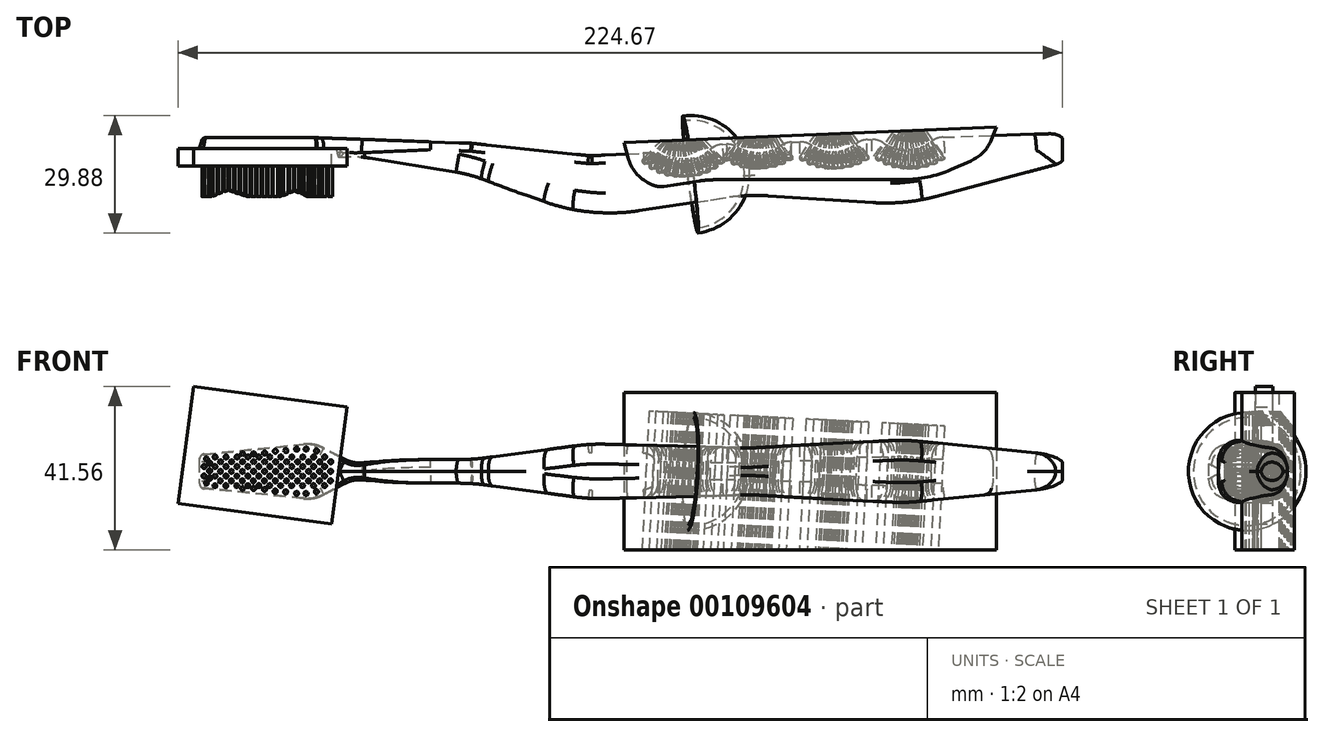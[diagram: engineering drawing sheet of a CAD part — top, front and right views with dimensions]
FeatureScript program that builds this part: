
annotation { "Feature Type Name" : "Feature", "Feature Type Description" : "" }
export const myFeature = defineFeature(function(context is Context, id is Id, definition is map)
    precondition{}
    {
        {
            var Q0;
            Q0=qCreatedBy(makeId("Front.planeOp"),FACE);
            var sketch = newSketch(context, id + "F0", { "sketchPlane" : qUnion([Q0])});
            skLineSegment(sketch, "E0", {"start": v(0, 0) * mm, "end": v(-220, 0) * mm, "construction": true});
            skLineSegment(sketch, "E1", {"start": v(-220, 0) * mm, "end": v(-220, 5) * mm});
            skLineSegment(sketch, "E2", {"start": v(-190, 0) * mm, "end": v(-190, 8) * mm, "construction": true});
            skLineSegment(sketch, "E3", {"start": v(-180, 0) * mm, "end": v(-180, 3) * mm, "construction": true});
            skLineSegment(sketch, "E4", {"start": v(-150, 0) * mm, "end": v(-150, 3) * mm, "construction": true});
            skLineSegment(sketch, "E5", {"start": v(-120, 0) * mm, "end": v(-120, 7) * mm, "construction": true});
            skLineSegment(sketch, "E6", {"start": v(-80, 0) * mm, "end": v(-80, 6) * mm, "construction": true});
            skLineSegment(sketch, "E7", {"start": v(-40, 0) * mm, "end": v(-40, 8) * mm, "construction": true});
            skLineSegment(sketch, "E8", {"start": v(0, 0) * mm, "end": v(0, 4) * mm});
            skLineSegment(sketch, "E9", {"start": v(0, 4) * mm, "end": v(-40, 8) * mm});
            skLineSegment(sketch, "E10", {"start": v(-40, 8) * mm, "end": v(-80, 6) * mm});
            skLineSegment(sketch, "E11", {"start": v(-80, 6) * mm, "end": v(-120, 7) * mm});
            skLineSegment(sketch, "E12", {"start": v(-120, 7) * mm, "end": v(-150, 3) * mm});
            skLineSegment(sketch, "E13", {"start": v(-150, 3) * mm, "end": v(-180, 3) * mm});
            skLineSegment(sketch, "E14", {"start": v(-180, 3) * mm, "end": v(-190, 8) * mm});
            skLineSegment(sketch, "E15", {"start": v(-190, 8) * mm, "end": v(-220, 5) * mm});
            skLineSegment(sketch, "E16.MirrorCS", {"start": v(0, 0) * mm, "end": v(0, -4) * mm});
            skLineSegment(sketch, "E17.MirrorCS", {"start": v(-220, 0) * mm, "end": v(-220, -5) * mm});
            skLineSegment(sketch, "E18.MirrorCS", {"start": v(-190, -8) * mm, "end": v(-220, -5) * mm});
            skLineSegment(sketch, "E19.MirrorCS", {"start": v(-180, -3) * mm, "end": v(-190, -8) * mm});
            skLineSegment(sketch, "E20.MirrorCS", {"start": v(-150, -3) * mm, "end": v(-180, -3) * mm});
            skLineSegment(sketch, "E21.MirrorCS", {"start": v(-120, -7) * mm, "end": v(-150, -3) * mm});
            skLineSegment(sketch, "E22.MirrorCS", {"start": v(-80, -6) * mm, "end": v(-120, -7) * mm});
            skLineSegment(sketch, "E23.MirrorCS", {"start": v(0, -4) * mm, "end": v(-40, -8) * mm});
            skLineSegment(sketch, "E24.MirrorCS", {"start": v(-40, -8) * mm, "end": v(-80, -6) * mm});
            skSolve(sketch);
        }
        {
            var Q0;
            Q0=makeQuery(id+"F0.imprint","IMPRINT",FACE,{"disambiguationData":[TD([[makeQuery(id+"F0.imprint","IMPRINT",EDGE,{"derivedFrom":sQuery(id+"F0.wireOp",EDGE,"E1")}),-1.0]])]});
            extrude(context, id + "F1", {"entities" : qUnion([Q0]), "depth" : 25 * mm});
        }
        {
            var Q0;
            Q0=makeQuery(id+"F1.opExtrude","SWEPT_FACE",FACE,{"disambiguationData":[OSD([sQuery(id+"F0.wireOp",EDGE,"E20.MirrorCS")])]});
            var sketch = newSketch(context, id + "F2", { "sketchPlane" : qUnion([Q0])});
            skLineSegment(sketch, "E25.0", {"start": v(-190, 0) * mm, "end": v(-220, 0) * mm, "construction": true});
            skLineSegment(sketch, "E25.4", {"start": v(-80, 0) * mm, "end": v(-120, 0) * mm, "construction": true});
            skLineSegment(sketch, "E25.5", {"start": v(-40, 0) * mm, "end": v(-80, 0) * mm, "construction": true});
            skLineSegment(sketch, "E25.6", {"start": v(0, 0) * mm, "end": v(-40, 0) * mm, "construction": true});
            skLineSegment(sketch, "E26", {"start": v(-220, 7.68) * mm, "end": v(-218.46, 2.68) * mm});
            skLineSegment(sketch, "E27", {"start": v(-218.46, 2.68) * mm, "end": v(-190, 2.68) * mm});
            skLineSegment(sketch, "E28", {"start": v(-119.9, 7.3) * mm, "end": v(-102.9, 6.47) * mm});
            skLineSegment(sketch, "E29", {"start": v(-119.9, 23.1) * mm, "end": v(-80, 17.11) * mm});
            skLineSegment(sketch, "E30", {"start": v(-80, 17.11) * mm, "end": v(-40, 19.71) * mm});
            skLineSegment(sketch, "E31", {"start": v(-40, 19.71) * mm, "end": v(0, 9.1) * mm});
            skLineSegment(sketch, "E32", {"start": v(0, 9.1) * mm, "end": v(0, 1.58) * mm});
            skArc(sketch, "E33", {"start": v(-88.51, 4.45) * mm, "mid": v(-95.27, 8.57) * mm, "end": v(-102.9, 6.47) * mm});
            skArc(sketch, "E34", {"start": v(-32.26, 2.63) * mm, "mid": v(-39.34, 5.9) * mm, "end": v(-46.62, 3.1) * mm});
            skLineSegment(sketch, "E35", {"start": v(-88.51, 4.45) * mm, "end": v(-83.73, 4.3) * mm});
            skLineSegment(sketch, "E36", {"start": v(-70.5, 3.87) * mm, "end": v(-64.85, 3.69) * mm});
            skArc(sketch, "E37.trimOffspring", {"start": v(-70.5, 3.87) * mm, "mid": v(-77.03, 6.54) * mm, "end": v(-83.73, 4.3) * mm});
            skLineSegment(sketch, "E38.trimOffspring", {"start": v(-51.47, 3.25) * mm, "end": v(-46.62, 3.1) * mm});
            skLineSegment(sketch, "E39.trimOffspring", {"start": v(-32.26, 2.63) * mm, "end": v(0, 1.58) * mm});
            skArc(sketch, "E40.trimOffspring", {"start": v(-51.47, 3.25) * mm, "mid": v(-58.07, 6.39) * mm, "end": v(-64.85, 3.69) * mm});
            skPoint(sketch, "E41.center.orphan", {"position": v(-77.66, -2.25) * mm});
            skPoint(sketch, "E42.center.orphan", {"position": v(-58.66, -3.17) * mm});
            skLineSegment(sketch, "E43.top", {"start": v(-229.41, 31.75) * mm, "end": v(15.55, 31.75) * mm});
            skLineSegment(sketch, "E43.left", {"start": v(-229.41, -17.07) * mm, "end": v(-229.41, 31.75) * mm});
            skLineSegment(sketch, "E43.right", {"start": v(15.55, -17.07) * mm, "end": v(15.55, 31.75) * mm});
            skLineSegment(sketch, "E44", {"start": v(-220, 7.68) * mm, "end": v(-180, 7.68) * mm});
            skLineSegment(sketch, "E45", {"start": v(-180, 7.68) * mm, "end": v(-150, 12.5) * mm});
            skLineSegment(sketch, "E46", {"start": v(-150, 12.5) * mm, "end": v(-119.9, 23.1) * mm});
            skLineSegment(sketch, "E47", {"start": v(-119.9, 7.3) * mm, "end": v(-150, 4.12) * mm});
            skLineSegment(sketch, "E48", {"start": v(-150, 4.12) * mm, "end": v(-190, 2.68) * mm});
            skLineSegment(sketch, "E49", {"start": v(15.55, -17.07) * mm, "end": v(-229.41, -17.07) * mm});
            skSolve(sketch);
        }
        {
            var Q0;
            Q0=makeQuery(id+"F2.imprint","IMPRINT",FACE,{"disambiguationData":[TD([[makeQuery(id+"F2.imprint","IMPRINT",EDGE,{"derivedFrom":sQuery(id+"F2.wireOp",EDGE,"E26")}),-1.0]])]});
            var Q1;
            {var subQ0=sQuery(id+"F2.wireOp",EDGE,"E45");Q1=makeQuery(id+"F2.imprint","IMPRINT",FACE,{"disambiguationData":[TD([[makeQuery(id+"F2.imprint","IMPRINT",EDGE,{"derivedFrom":subQ0}),1.0]])]});}
            var Q2;
            {var subQ1=sQuery(id+"F0.wireOp",EDGE,"E20.MirrorCS");var subQ6=makeQuery(id+"F1.opExtrude","CAP_EDGE",EDGE,{"disambiguationData":[OSD([subQ1])],"isStart":true});Q2=makeQuery(id+"F2.imprint","IMPRINT",FACE,{"disambiguationData":[TD([[makeQuery(id+"F2.imprint","IMPRINT",EDGE,{"derivedFrom":subQ6}),-1.0]])]});}
            extrude(context, id + "F3", {"entities" : qUnion([Q0, Q1, Q2]), "operationType" : NewBodyOperationType.REMOVE, "endBound" : BoundingType.SYMMETRIC, "oppositeDirection" : true, "depth" : 40 * mm});
        }
        {
            var Q0;
            Q0=makeQuery(id+"F3.boolean.opBoolean","COPY",EDGE,{"derivedFrom":makeQuery(id+"F3.opExtrude","SWEPT_EDGE",EDGE,{"disambiguationData":[OSD([sQuery(id+"F2.wireOp",EDGE,"E29"),sQuery(id+"F2.wireOp",EDGE,"E46")])]})});
            var Q1;
            Q1=makeQuery(id+"F3.boolean.opBoolean","COPY",EDGE,{"derivedFrom":makeQuery(id+"F3.opExtrude","SWEPT_EDGE",EDGE,{"disambiguationData":[OSD([sQuery(id+"F2.wireOp",EDGE,"E29"),sQuery(id+"F2.wireOp",EDGE,"E30")])]})});
            var Q2;
            Q2=makeQuery(id+"F3.boolean.opBoolean","COPY",EDGE,{"derivedFrom":makeQuery(id+"F3.opExtrude","SWEPT_EDGE",EDGE,{"disambiguationData":[OSD([sQuery(id+"F2.wireOp",EDGE,"E30"),sQuery(id+"F2.wireOp",EDGE,"E31")])]})});
            var Q3;
            Q3=makeQuery(id+"F3.boolean.opBoolean","COPY",EDGE,{"derivedFrom":makeQuery(id+"F3.opExtrude","SWEPT_EDGE",EDGE,{"disambiguationData":[OSD([sQuery(id+"F0.wireOp",EDGE,"E20.MirrorCS"),sQuery(id+"F0.wireOp",EDGE,"E21.MirrorCS"),sQuery(id+"F2.wireOp",EDGE,"E45"),sQuery(id+"F2.wireOp",EDGE,"E46")])]})});
            var Q4;
            Q4=makeQuery(id+"F3.boolean.opBoolean","COPY",EDGE,{"derivedFrom":makeQuery(id+"F3.opExtrude","SWEPT_EDGE",EDGE,{"disambiguationData":[OSD([sQuery(id+"F0.wireOp",EDGE,"E19.MirrorCS"),sQuery(id+"F0.wireOp",EDGE,"E20.MirrorCS"),sQuery(id+"F2.wireOp",EDGE,"E44"),sQuery(id+"F2.wireOp",EDGE,"E45")])]})});
            fillet(context, id + "F4", {"entities" : qUnion([Q0, Q1, Q2, Q3, Q4]), "radius" : 50 * mm, "tangentPropagation" : true, "allowEdgeOverflow" : false});
        }
        {
            var Q0;
            Q0=makeQuery(id+"F3.boolean.opBoolean","COPY",EDGE,{"derivedFrom":makeQuery(id+"F3.opExtrude","SWEPT_EDGE",EDGE,{"disambiguationData":[OSD([sQuery(id+"F2.wireOp",EDGE,"E27"),sQuery(id+"F2.wireOp",EDGE,"E48")])]})});
            var Q1;
            Q1=makeQuery(id+"F3.boolean.opBoolean","COPY",EDGE,{"derivedFrom":makeQuery(id+"F3.opExtrude","SWEPT_EDGE",EDGE,{"disambiguationData":[OSD([sQuery(id+"F0.wireOp",EDGE,"E20.MirrorCS"),sQuery(id+"F0.wireOp",EDGE,"E21.MirrorCS"),sQuery(id+"F2.wireOp",EDGE,"E47"),sQuery(id+"F2.wireOp",EDGE,"E48")])]})});
            var Q2;
            Q2=makeQuery(id+"F3.boolean.opBoolean","COPY",EDGE,{"derivedFrom":makeQuery(id+"F3.opExtrude","SWEPT_EDGE",EDGE,{"disambiguationData":[OSD([sQuery(id+"F2.wireOp",EDGE,"E28"),sQuery(id+"F2.wireOp",EDGE,"E47")])]})});
            fillet(context, id + "F5", {"entities" : qUnion([Q0, Q1, Q2]), "radius" : 5 * mm, "tangentPropagation" : true, "allowEdgeOverflow" : false});
        }
        {
            var Q0;
            Q0=makeQuery(id+"F1.opExtrude","SWEPT_EDGE",EDGE,{"disambiguationData":[OSD([sQuery(id+"F0.wireOp",EDGE,"E20.MirrorCS"),sQuery(id+"F0.wireOp",EDGE,"E21.MirrorCS")])]});
            var Q1;
            Q1=makeQuery(id+"F1.opExtrude","SWEPT_EDGE",EDGE,{"disambiguationData":[OSD([sQuery(id+"F0.wireOp",EDGE,"E21.MirrorCS"),sQuery(id+"F0.wireOp",EDGE,"E22.MirrorCS")])]});
            var Q2;
            Q2=makeQuery(id+"F1.opExtrude","SWEPT_EDGE",EDGE,{"disambiguationData":[OSD([sQuery(id+"F0.wireOp",EDGE,"E22.MirrorCS"),sQuery(id+"F0.wireOp",EDGE,"E24.MirrorCS")])]});
            var Q3;
            Q3=makeQuery(id+"F1.opExtrude","SWEPT_EDGE",EDGE,{"disambiguationData":[OSD([sQuery(id+"F0.wireOp",EDGE,"E23.MirrorCS"),sQuery(id+"F0.wireOp",EDGE,"E24.MirrorCS")])]});
            var Q4;
            Q4=makeQuery(id+"F1.opExtrude","SWEPT_EDGE",EDGE,{"disambiguationData":[OSD([sQuery(id+"F0.wireOp",EDGE,"E12"),sQuery(id+"F0.wireOp",EDGE,"E13")])]});
            var Q5;
            Q5=makeQuery(id+"F1.opExtrude","SWEPT_EDGE",EDGE,{"disambiguationData":[OSD([sQuery(id+"F0.wireOp",EDGE,"E11"),sQuery(id+"F0.wireOp",EDGE,"E12")])]});
            var Q6;
            Q6=makeQuery(id+"F1.opExtrude","SWEPT_EDGE",EDGE,{"disambiguationData":[OSD([sQuery(id+"F0.wireOp",EDGE,"E10"),sQuery(id+"F0.wireOp",EDGE,"E11")])]});
            var Q7;
            Q7=makeQuery(id+"F1.opExtrude","SWEPT_EDGE",EDGE,{"disambiguationData":[OSD([sQuery(id+"F0.wireOp",EDGE,"E9"),sQuery(id+"F0.wireOp",EDGE,"E10")])]});
            fillet(context, id + "F6", {"entities" : qUnion([Q0, Q1, Q2, Q3, Q4, Q5, Q6, Q7]), "radius" : 50 * mm, "tangentPropagation" : true, "allowEdgeOverflow" : false});
        }
        {
            var Q0;
            Q0=makeQuery(id+"F1.opExtrude","SWEPT_EDGE",EDGE,{"disambiguationData":[OSD([sQuery(id+"F0.wireOp",EDGE,"E18.MirrorCS"),sQuery(id+"F0.wireOp",EDGE,"E19.MirrorCS")])]});
            var Q1;
            Q1=makeQuery(id+"F1.opExtrude","SWEPT_EDGE",EDGE,{"disambiguationData":[OSD([sQuery(id+"F0.wireOp",EDGE,"E19.MirrorCS"),sQuery(id+"F0.wireOp",EDGE,"E20.MirrorCS")])]});
            var Q2;
            Q2=makeQuery(id+"F1.opExtrude","SWEPT_EDGE",EDGE,{"disambiguationData":[OSD([sQuery(id+"F0.wireOp",EDGE,"E13"),sQuery(id+"F0.wireOp",EDGE,"E14")])]});
            var Q3;
            Q3=makeQuery(id+"F1.opExtrude","SWEPT_EDGE",EDGE,{"disambiguationData":[OSD([sQuery(id+"F0.wireOp",EDGE,"E14"),sQuery(id+"F0.wireOp",EDGE,"E15")])]});
            fillet(context, id + "F7", {"entities" : qUnion([Q0, Q1, Q2, Q3]), "radius" : 10 * mm, "tangentPropagation" : true, "allowEdgeOverflow" : false});
        }
        {
            var Q0;
            Q0=makeQuery(id+"F6.opFillet","BLEND_EDGE",EDGE,{"blendedFrom":[makeQuery(id+"F1.opExtrude","SWEPT_EDGE",EDGE,{"disambiguationData":[OSD([sQuery(id+"F0.wireOp",EDGE,"E21.MirrorCS"),sQuery(id+"F0.wireOp",EDGE,"E22.MirrorCS")])]}),makeQuery(id+"F4.opFillet","BLEND_FACE",FACE,{"disambiguationData":[OSD([sQuery(id+"F2.wireOp",EDGE,"E29"),sQuery(id+"F2.wireOp",EDGE,"E46")])]})],"blendedInto":[makeQuery(id+"F4.opFillet","BLEND_FACE",FACE,{"disambiguationData":[OSD([sQuery(id+"F2.wireOp",EDGE,"E29"),sQuery(id+"F2.wireOp",EDGE,"E46")])]})]});
            var Q1;
            Q1=makeQuery(id+"F3.boolean.opBoolean","INTERSECT",EDGE,{"derivedFrom":[makeQuery(id+"F1.opExtrude","SWEPT_FACE",FACE,{"disambiguationData":[OSD([sQuery(id+"F0.wireOp",EDGE,"E11")])]}),makeQuery(id+"F3.opExtrude","SWEPT_FACE",FACE,{"disambiguationData":[OSD([sQuery(id+"F2.wireOp",EDGE,"E29")])]})]});
            fillet(context, id + "F8", {"entities" : qUnion([Q0, Q1]), "radius" : 5 * mm, "tangentPropagation" : true, "allowEdgeOverflow" : false});
        }
        {
            var Q0;
            Q0=makeQuery(id+"F3.boolean.opBoolean","INTERSECT",EDGE,{"derivedFrom":[makeQuery(id+"F1.opExtrude","SWEPT_FACE",FACE,{"disambiguationData":[OSD([sQuery(id+"F0.wireOp",EDGE,"E22.MirrorCS")])]}),makeQuery(id+"F3.opExtrude","SWEPT_FACE",FACE,{"disambiguationData":[OSD([sQuery(id+"F2.wireOp",EDGE,"E33")])]})]});
            var Q1;
            Q1=makeQuery(id+"F6.opFillet","BLEND_EDGE",EDGE,{"blendedFrom":[makeQuery(id+"F1.opExtrude","SWEPT_EDGE",EDGE,{"disambiguationData":[OSD([sQuery(id+"F0.wireOp",EDGE,"E22.MirrorCS"),sQuery(id+"F0.wireOp",EDGE,"E24.MirrorCS")])]}),makeQuery(id+"F3.boolean.opBoolean","COPY",FACE,{"derivedFrom":makeQuery(id+"F3.opExtrude","SWEPT_FACE",FACE,{"disambiguationData":[OSD([sQuery(id+"F2.wireOp",EDGE,"E37.trimOffspring")])]})})],"blendedInto":[makeQuery(id+"F3.boolean.opBoolean","COPY",FACE,{"derivedFrom":makeQuery(id+"F3.opExtrude","SWEPT_FACE",FACE,{"disambiguationData":[OSD([sQuery(id+"F2.wireOp",EDGE,"E37.trimOffspring")])]})})]});
            var Q2;
            Q2=makeQuery(id+"F3.boolean.opBoolean","INTERSECT",EDGE,{"derivedFrom":[makeQuery(id+"F1.opExtrude","SWEPT_FACE",FACE,{"disambiguationData":[OSD([sQuery(id+"F0.wireOp",EDGE,"E24.MirrorCS")])]}),makeQuery(id+"F3.opExtrude","SWEPT_FACE",FACE,{"disambiguationData":[OSD([sQuery(id+"F2.wireOp",EDGE,"E40.trimOffspring")])]})]});
            var Q3;
            Q3=makeQuery(id+"F6.opFillet","BLEND_EDGE",EDGE,{"blendedFrom":[makeQuery(id+"F1.opExtrude","SWEPT_EDGE",EDGE,{"disambiguationData":[OSD([sQuery(id+"F0.wireOp",EDGE,"E23.MirrorCS"),sQuery(id+"F0.wireOp",EDGE,"E24.MirrorCS")])]}),makeQuery(id+"F3.boolean.opBoolean","COPY",FACE,{"derivedFrom":makeQuery(id+"F3.opExtrude","SWEPT_FACE",FACE,{"disambiguationData":[OSD([sQuery(id+"F2.wireOp",EDGE,"E34")])]})})],"blendedInto":[makeQuery(id+"F3.boolean.opBoolean","COPY",FACE,{"derivedFrom":makeQuery(id+"F3.opExtrude","SWEPT_FACE",FACE,{"disambiguationData":[OSD([sQuery(id+"F2.wireOp",EDGE,"E34")])]})})]});
            var Q4;
            Q4=makeQuery(id+"F3.boolean.opBoolean","INTERSECT",EDGE,{"derivedFrom":[makeQuery(id+"F1.opExtrude","SWEPT_FACE",FACE,{"disambiguationData":[OSD([sQuery(id+"F0.wireOp",EDGE,"E22.MirrorCS")])]}),makeQuery(id+"F3.opExtrude","SWEPT_FACE",FACE,{"disambiguationData":[OSD([sQuery(id+"F2.wireOp",EDGE,"E35")])]})]});
            var Q5;
            Q5=makeQuery(id+"F3.boolean.opBoolean","INTERSECT",EDGE,{"derivedFrom":[makeQuery(id+"F1.opExtrude","SWEPT_FACE",FACE,{"disambiguationData":[OSD([sQuery(id+"F0.wireOp",EDGE,"E24.MirrorCS")])]}),makeQuery(id+"F3.opExtrude","SWEPT_FACE",FACE,{"disambiguationData":[OSD([sQuery(id+"F2.wireOp",EDGE,"E36")])]})]});
            var Q6;
            Q6=makeQuery(id+"F3.boolean.opBoolean","INTERSECT",EDGE,{"derivedFrom":[makeQuery(id+"F1.opExtrude","SWEPT_FACE",FACE,{"disambiguationData":[OSD([sQuery(id+"F0.wireOp",EDGE,"E24.MirrorCS")])]}),makeQuery(id+"F3.opExtrude","SWEPT_FACE",FACE,{"disambiguationData":[OSD([sQuery(id+"F2.wireOp",EDGE,"E38.trimOffspring")])]})]});
            var Q7;
            Q7=makeQuery(id+"F3.boolean.opBoolean","INTERSECT",EDGE,{"derivedFrom":[makeQuery(id+"F1.opExtrude","SWEPT_FACE",FACE,{"disambiguationData":[OSD([sQuery(id+"F0.wireOp",EDGE,"E23.MirrorCS")])]}),makeQuery(id+"F3.opExtrude","SWEPT_FACE",FACE,{"disambiguationData":[OSD([sQuery(id+"F2.wireOp",EDGE,"E39.trimOffspring")])]})]});
            var Q8;
            Q8=makeQuery(id+"F3.boolean.opBoolean","INTERSECT",EDGE,{"derivedFrom":[makeQuery(id+"F1.opExtrude","SWEPT_FACE",FACE,{"disambiguationData":[OSD([sQuery(id+"F0.wireOp",EDGE,"E11")])]}),makeQuery(id+"F3.opExtrude","SWEPT_FACE",FACE,{"disambiguationData":[OSD([sQuery(id+"F2.wireOp",EDGE,"E33")])]})]});
            var Q9;
            Q9=makeQuery(id+"F3.boolean.opBoolean","INTERSECT",EDGE,{"derivedFrom":[makeQuery(id+"F1.opExtrude","SWEPT_FACE",FACE,{"disambiguationData":[OSD([sQuery(id+"F0.wireOp",EDGE,"E11")])]}),makeQuery(id+"F3.opExtrude","SWEPT_FACE",FACE,{"disambiguationData":[OSD([sQuery(id+"F2.wireOp",EDGE,"E35")])]})]});
            var Q10;
            Q10=makeQuery(id+"F3.boolean.opBoolean","INTERSECT",EDGE,{"derivedFrom":[makeQuery(id+"F1.opExtrude","SWEPT_FACE",FACE,{"disambiguationData":[OSD([sQuery(id+"F0.wireOp",EDGE,"E10")])]}),makeQuery(id+"F3.opExtrude","SWEPT_FACE",FACE,{"disambiguationData":[OSD([sQuery(id+"F2.wireOp",EDGE,"E37.trimOffspring")])]})]});
            var Q11;
            Q11=makeQuery(id+"F3.boolean.opBoolean","INTERSECT",EDGE,{"derivedFrom":[makeQuery(id+"F1.opExtrude","SWEPT_FACE",FACE,{"disambiguationData":[OSD([sQuery(id+"F0.wireOp",EDGE,"E10")])]}),makeQuery(id+"F3.opExtrude","SWEPT_FACE",FACE,{"disambiguationData":[OSD([sQuery(id+"F2.wireOp",EDGE,"E36")])]})]});
            var Q12;
            Q12=makeQuery(id+"F3.boolean.opBoolean","INTERSECT",EDGE,{"derivedFrom":[makeQuery(id+"F1.opExtrude","SWEPT_FACE",FACE,{"disambiguationData":[OSD([sQuery(id+"F0.wireOp",EDGE,"E10")])]}),makeQuery(id+"F3.opExtrude","SWEPT_FACE",FACE,{"disambiguationData":[OSD([sQuery(id+"F2.wireOp",EDGE,"E40.trimOffspring")])]})]});
            var Q13;
            Q13=makeQuery(id+"F3.boolean.opBoolean","INTERSECT",EDGE,{"derivedFrom":[makeQuery(id+"F1.opExtrude","SWEPT_FACE",FACE,{"disambiguationData":[OSD([sQuery(id+"F0.wireOp",EDGE,"E10")])]}),makeQuery(id+"F3.opExtrude","SWEPT_FACE",FACE,{"disambiguationData":[OSD([sQuery(id+"F2.wireOp",EDGE,"E38.trimOffspring")])]})]});
            var Q14;
            Q14=makeQuery(id+"F6.opFillet","BLEND_EDGE",EDGE,{"blendedFrom":[makeQuery(id+"F1.opExtrude","SWEPT_EDGE",EDGE,{"disambiguationData":[OSD([sQuery(id+"F0.wireOp",EDGE,"E9"),sQuery(id+"F0.wireOp",EDGE,"E10")])]}),makeQuery(id+"F3.boolean.opBoolean","COPY",FACE,{"derivedFrom":makeQuery(id+"F3.opExtrude","SWEPT_FACE",FACE,{"disambiguationData":[OSD([sQuery(id+"F2.wireOp",EDGE,"E34")])]})})],"blendedInto":[makeQuery(id+"F3.boolean.opBoolean","COPY",FACE,{"derivedFrom":makeQuery(id+"F3.opExtrude","SWEPT_FACE",FACE,{"disambiguationData":[OSD([sQuery(id+"F2.wireOp",EDGE,"E34")])]})})]});
            var Q15;
            Q15=makeQuery(id+"F3.boolean.opBoolean","INTERSECT",EDGE,{"derivedFrom":[makeQuery(id+"F1.opExtrude","SWEPT_FACE",FACE,{"disambiguationData":[OSD([sQuery(id+"F0.wireOp",EDGE,"E9")])]}),makeQuery(id+"F3.opExtrude","SWEPT_FACE",FACE,{"disambiguationData":[OSD([sQuery(id+"F2.wireOp",EDGE,"E39.trimOffspring")])]})]});
            fillet(context, id + "F9", {"entities" : qUnion([Q0, Q1, Q2, Q3, Q4, Q5, Q6, Q7, Q8, Q9, Q10, Q11, Q12, Q13, Q14, Q15]), "radius" : 4 * mm, "tangentPropagation" : true, "allowEdgeOverflow" : false});
        }
        {
            var Q0;
            Q0=makeQuery(id+"F3.boolean.opBoolean","INTERSECT",EDGE,{"derivedFrom":[makeQuery(id+"F1.opExtrude","SWEPT_FACE",FACE,{"disambiguationData":[OSD([sQuery(id+"F0.wireOp",EDGE,"E22.MirrorCS")])]}),makeQuery(id+"F3.opExtrude","SWEPT_FACE",FACE,{"disambiguationData":[OSD([sQuery(id+"F2.wireOp",EDGE,"E28")])]})]});
            fillet(context, id + "F10", {"entities" : qUnion([Q0]), "radius" : 2 * mm, "tangentPropagation" : true, "allowEdgeOverflow" : false});
        }
        {
            var Q0;
            Q0=makeQuery(id+"F3.boolean.opBoolean","COPY",EDGE,{"derivedFrom":makeQuery(id+"F3.opExtrude","SWEPT_EDGE",EDGE,{"disambiguationData":[OSD([sQuery(id+"F2.wireOp",EDGE,"E33"),sQuery(id+"F2.wireOp",EDGE,"E35")])]})});
            var Q1;
            Q1=makeQuery(id+"F3.boolean.opBoolean","COPY",EDGE,{"derivedFrom":makeQuery(id+"F3.opExtrude","SWEPT_EDGE",EDGE,{"disambiguationData":[OSD([sQuery(id+"F2.wireOp",EDGE,"E35"),sQuery(id+"F2.wireOp",EDGE,"E37.trimOffspring")])]})});
            var Q2;
            Q2=makeQuery(id+"F3.boolean.opBoolean","COPY",EDGE,{"derivedFrom":makeQuery(id+"F3.opExtrude","SWEPT_EDGE",EDGE,{"disambiguationData":[OSD([sQuery(id+"F2.wireOp",EDGE,"E36"),sQuery(id+"F2.wireOp",EDGE,"E37.trimOffspring")])]})});
            var Q3;
            Q3=makeQuery(id+"F3.boolean.opBoolean","COPY",EDGE,{"derivedFrom":makeQuery(id+"F3.opExtrude","SWEPT_EDGE",EDGE,{"disambiguationData":[OSD([sQuery(id+"F2.wireOp",EDGE,"E36"),sQuery(id+"F2.wireOp",EDGE,"E40.trimOffspring")])]})});
            var Q4;
            Q4=makeQuery(id+"F3.boolean.opBoolean","COPY",EDGE,{"derivedFrom":makeQuery(id+"F3.opExtrude","SWEPT_EDGE",EDGE,{"disambiguationData":[OSD([sQuery(id+"F2.wireOp",EDGE,"E38.trimOffspring"),sQuery(id+"F2.wireOp",EDGE,"E40.trimOffspring")])]})});
            var Q5;
            Q5=makeQuery(id+"F3.boolean.opBoolean","COPY",EDGE,{"derivedFrom":makeQuery(id+"F3.opExtrude","SWEPT_EDGE",EDGE,{"disambiguationData":[OSD([sQuery(id+"F2.wireOp",EDGE,"E34"),sQuery(id+"F2.wireOp",EDGE,"E38.trimOffspring")])]})});
            var Q6;
            Q6=makeQuery(id+"F3.boolean.opBoolean","COPY",EDGE,{"derivedFrom":makeQuery(id+"F3.opExtrude","SWEPT_EDGE",EDGE,{"disambiguationData":[OSD([sQuery(id+"F2.wireOp",EDGE,"E34"),sQuery(id+"F2.wireOp",EDGE,"E39.trimOffspring")])]})});
            fillet(context, id + "F11", {"entities" : qUnion([Q0, Q1, Q2, Q3, Q4, Q5, Q6]), "radius" : 5 * mm, "tangentPropagation" : true, "allowEdgeOverflow" : false});
        }
        {
            var Q0;
            Q0=makeQuery(id+"F8.opFillet","BLEND_EDGE",EDGE,{"blendedFrom":[makeQuery(id+"F3.boolean.opBoolean","INTERSECT",EDGE,{"derivedFrom":[makeQuery(id+"F1.opExtrude","SWEPT_FACE",FACE,{"disambiguationData":[OSD([sQuery(id+"F0.wireOp",EDGE,"E18.MirrorCS")])]}),makeQuery(id+"F3.opExtrude","SWEPT_FACE",FACE,{"disambiguationData":[OSD([sQuery(id+"F2.wireOp",EDGE,"E44")])]})]}),makeQuery(id+"F3.boolean.opBoolean","COPY",FACE,{"derivedFrom":makeQuery(id+"F3.opExtrude","SWEPT_FACE",FACE,{"disambiguationData":[OSD([sQuery(id+"F2.wireOp",EDGE,"E26")])]})})],"blendedInto":[makeQuery(id+"F3.boolean.opBoolean","COPY",FACE,{"derivedFrom":makeQuery(id+"F3.opExtrude","SWEPT_FACE",FACE,{"disambiguationData":[OSD([sQuery(id+"F2.wireOp",EDGE,"E26")])]})})]});
            fillet(context, id + "F12", {"entities" : qUnion([Q0]), "radius" : 1 * mm, "tangentPropagation" : true, "allowEdgeOverflow" : false});
        }
        {
            var Q0;
            Q0=qCreatedBy(makeId("Top.planeOp"),FACE);
            var sketch = newSketch(context, id + "F13", { "sketchPlane" : qUnion([Q0])});
            skLineSegment(sketch, "E50", {"start": v(-111.36, -3.91) * mm, "end": v(-110.38, -7.71) * mm});
            skLineSegment(sketch, "E51", {"start": v(-104.93, -14.29) * mm, "end": v(-104.14, -14.66) * mm});
            skLineSegment(sketch, "E52", {"start": v(-101.27, -15.07) * mm, "end": v(-92.35, -13.7) * mm});
            skLineSegment(sketch, "E53", {"start": v(-87.82, -13.36) * mm, "end": v(-74.2, -13.36) * mm});
            skLineSegment(sketch, "E54", {"start": v(-74.2, -13.36) * mm, "end": v(-53.16, -13.36) * mm});
            skLineSegment(sketch, "E55", {"start": v(-53.16, -13.36) * mm, "end": v(-40.43, -13.36) * mm});
            skLineSegment(sketch, "E56", {"start": v(-28.35, -10.83) * mm, "end": v(-23.32, -8.61) * mm});
            skLineSegment(sketch, "E57", {"start": v(-18.04, -3.12) * mm, "end": v(-16.8, 0) * mm});
            skPoint(sketch, "E58.visualSharp", {"position": v(-109.21, -12.29) * mm});
            skArc(sketch, "E58.filletArc", {"start": v(-110.38, -7.71) * mm, "mid": v(-108.4, -11.61) * mm, "end": v(-104.93, -14.29) * mm});
            skPoint(sketch, "E59.visualSharp", {"position": v(-102.77, -15.3) * mm});
            skArc(sketch, "E59.filletArc", {"start": v(-104.14, -14.66) * mm, "mid": v(-102.74, -15.07) * mm, "end": v(-101.27, -15.07) * mm});
            skPoint(sketch, "E60.visualSharp", {"position": v(-19.55, -6.95) * mm});
            skArc(sketch, "E60.filletArc", {"start": v(-23.32, -8.61) * mm, "mid": v(-20.13, -6.39) * mm, "end": v(-18.04, -3.12) * mm});
            skPoint(sketch, "E61.visualSharp", {"position": v(-34.12, -13.36) * mm});
            skArc(sketch, "E61.filletArc", {"start": v(-40.43, -13.36) * mm, "mid": v(-34.26, -12.72) * mm, "end": v(-28.35, -10.83) * mm});
            skPoint(sketch, "E62.visualSharp", {"position": v(-90.1, -13.36) * mm});
            skArc(sketch, "E62.filletArc", {"start": v(-87.82, -13.36) * mm, "mid": v(-90.1, -13.45) * mm, "end": v(-92.35, -13.7) * mm});
            skLineSegment(sketch, "E63", {"start": v(-111.36, -3.91) * mm, "end": v(-16.8, 0) * mm});
            skSolve(sketch);
        }
        {
            var Q0;
            Q0=makeQuery(id+"F13.imprint","IMPRINT",FACE,{"disambiguationData":[TD([[makeQuery(id+"F13.imprint","IMPRINT",EDGE,{"derivedFrom":sQuery(id+"F13.wireOp",EDGE,"E50")}),1.0]])]});
            extrude(context, id + "F14", {"entities" : qUnion([Q0]), "endBound" : BoundingType.SYMMETRIC, "depth" : 40 * mm});
        }
        {
            var Q0;
            Q0=makeQuery(id+"F14.opExtrude","SWEPT_BODY",BODY,{"disambiguationData":[OSD([sQuery(id+"F13.wireOp",EDGE,"E50"),sQuery(id+"F13.wireOp",EDGE,"E51"),sQuery(id+"F13.wireOp",EDGE,"E52"),sQuery(id+"F13.wireOp",EDGE,"E53"),sQuery(id+"F13.wireOp",EDGE,"E54"),sQuery(id+"F13.wireOp",EDGE,"E55"),sQuery(id+"F13.wireOp",EDGE,"E56"),sQuery(id+"F13.wireOp",EDGE,"E57"),sQuery(id+"F13.wireOp",EDGE,"E58.filletArc"),sQuery(id+"F13.wireOp",EDGE,"E59.filletArc"),sQuery(id+"F13.wireOp",EDGE,"E60.filletArc"),sQuery(id+"F13.wireOp",EDGE,"E61.filletArc"),sQuery(id+"F13.wireOp",EDGE,"E62.filletArc"),sQuery(id+"F13.wireOp",EDGE,"E63")])]});
            var Q1;
            Q1=makeQuery(id+"F1.opExtrude","SWEPT_BODY",BODY,{"disambiguationData":[OSD([sQuery(id+"F0.wireOp",EDGE,"E1"),sQuery(id+"F0.wireOp",EDGE,"E8"),sQuery(id+"F0.wireOp",EDGE,"E9"),sQuery(id+"F0.wireOp",EDGE,"E10"),sQuery(id+"F0.wireOp",EDGE,"E11"),sQuery(id+"F0.wireOp",EDGE,"E12"),sQuery(id+"F0.wireOp",EDGE,"E13"),sQuery(id+"F0.wireOp",EDGE,"E14"),sQuery(id+"F0.wireOp",EDGE,"E15"),sQuery(id+"F0.wireOp",EDGE,"E16.MirrorCS"),sQuery(id+"F0.wireOp",EDGE,"E17.MirrorCS"),sQuery(id+"F0.wireOp",EDGE,"E18.MirrorCS"),sQuery(id+"F0.wireOp",EDGE,"E19.MirrorCS"),sQuery(id+"F0.wireOp",EDGE,"E20.MirrorCS"),sQuery(id+"F0.wireOp",EDGE,"E21.MirrorCS"),sQuery(id+"F0.wireOp",EDGE,"E22.MirrorCS"),sQuery(id+"F0.wireOp",EDGE,"E23.MirrorCS"),sQuery(id+"F0.wireOp",EDGE,"E24.MirrorCS")])]});
            booleanBodies(context, id + "F15", {"operationType" : BooleanOperationType.INTERSECTION, "tools" : qUnion([Q0, Q1]), "keepTools" : true});
        }
        {
            var Q0;
            Q0=makeQuery(id+"F15.opBoolean","INTERSECT",BODY,{"derivedFrom":[makeQuery(id+"F1.opExtrude","SWEPT_BODY",BODY,{"disambiguationData":[OSD([sQuery(id+"F0.wireOp",EDGE,"E1"),sQuery(id+"F0.wireOp",EDGE,"E8"),sQuery(id+"F0.wireOp",EDGE,"E9"),sQuery(id+"F0.wireOp",EDGE,"E10"),sQuery(id+"F0.wireOp",EDGE,"E11"),sQuery(id+"F0.wireOp",EDGE,"E12"),sQuery(id+"F0.wireOp",EDGE,"E13"),sQuery(id+"F0.wireOp",EDGE,"E14"),sQuery(id+"F0.wireOp",EDGE,"E15"),sQuery(id+"F0.wireOp",EDGE,"E16.MirrorCS"),sQuery(id+"F0.wireOp",EDGE,"E17.MirrorCS"),sQuery(id+"F0.wireOp",EDGE,"E18.MirrorCS"),sQuery(id+"F0.wireOp",EDGE,"E19.MirrorCS"),sQuery(id+"F0.wireOp",EDGE,"E20.MirrorCS"),sQuery(id+"F0.wireOp",EDGE,"E21.MirrorCS"),sQuery(id+"F0.wireOp",EDGE,"E22.MirrorCS"),sQuery(id+"F0.wireOp",EDGE,"E23.MirrorCS"),sQuery(id+"F0.wireOp",EDGE,"E24.MirrorCS")])]}),makeQuery(id+"F14.opExtrude","SWEPT_BODY",BODY,{"disambiguationData":[OSD([sQuery(id+"F13.wireOp",EDGE,"E50"),sQuery(id+"F13.wireOp",EDGE,"E51"),sQuery(id+"F13.wireOp",EDGE,"E52"),sQuery(id+"F13.wireOp",EDGE,"E53"),sQuery(id+"F13.wireOp",EDGE,"E54"),sQuery(id+"F13.wireOp",EDGE,"E55"),sQuery(id+"F13.wireOp",EDGE,"E56"),sQuery(id+"F13.wireOp",EDGE,"E57"),sQuery(id+"F13.wireOp",EDGE,"E58.filletArc"),sQuery(id+"F13.wireOp",EDGE,"E59.filletArc"),sQuery(id+"F13.wireOp",EDGE,"E60.filletArc"),sQuery(id+"F13.wireOp",EDGE,"E61.filletArc"),sQuery(id+"F13.wireOp",EDGE,"E62.filletArc"),sQuery(id+"F13.wireOp",EDGE,"E63")])]})]});
            var Q1;
            Q1=makeQuery(id+"F1.opExtrude","SWEPT_BODY",BODY,{"disambiguationData":[OSD([sQuery(id+"F0.wireOp",EDGE,"E1"),sQuery(id+"F0.wireOp",EDGE,"E8"),sQuery(id+"F0.wireOp",EDGE,"E9"),sQuery(id+"F0.wireOp",EDGE,"E10"),sQuery(id+"F0.wireOp",EDGE,"E11"),sQuery(id+"F0.wireOp",EDGE,"E12"),sQuery(id+"F0.wireOp",EDGE,"E13"),sQuery(id+"F0.wireOp",EDGE,"E14"),sQuery(id+"F0.wireOp",EDGE,"E15"),sQuery(id+"F0.wireOp",EDGE,"E16.MirrorCS"),sQuery(id+"F0.wireOp",EDGE,"E17.MirrorCS"),sQuery(id+"F0.wireOp",EDGE,"E18.MirrorCS"),sQuery(id+"F0.wireOp",EDGE,"E19.MirrorCS"),sQuery(id+"F0.wireOp",EDGE,"E20.MirrorCS"),sQuery(id+"F0.wireOp",EDGE,"E21.MirrorCS"),sQuery(id+"F0.wireOp",EDGE,"E22.MirrorCS"),sQuery(id+"F0.wireOp",EDGE,"E23.MirrorCS"),sQuery(id+"F0.wireOp",EDGE,"E24.MirrorCS")])]});
            booleanBodies(context, id + "F16", {"operationType" : BooleanOperationType.SUBTRACTION, "tools" : qUnion([Q0]), "targets" : qUnion([Q1]), "keepTools" : true});
        }
        {
            var Q0;
            Q0=makeQuery(id+"F15.opBoolean","COPY",FACE,{"derivedFrom":makeQuery(id+"F1.opExtrude","SWEPT_FACE",FACE,{"disambiguationData":[OSD([sQuery(id+"F0.wireOp",EDGE,"E24.MirrorCS")])]})});
            var sketch = newSketch(context, id + "F17", { "sketchPlane" : qUnion([Q0])});
            skEllipticalArc(sketch, "E64.0", {});
            skLineSegment(sketch, "E65", {"start": v(-96.12, -1.34) * mm, "end": v(-105.56, 8.28) * mm});
            skLineSegment(sketch, "E66", {"start": v(-96.12, -1.34) * mm, "end": v(-104.6, 9.15) * mm});
            skLineSegment(sketch, "E67.anchor1", {"start": v(-96.12, -1.34) * mm, "end": v(-96.12, -1.34) * mm});
            skLineSegment(sketch, "E67.anchor2", {"start": v(-96.12, -1.34) * mm, "end": v(-96.12, -1.34) * mm});
            skPoint(sketch, "E68.visualSharp", {"position": v(-104.91, 9.54) * mm});
            skArc(sketch, "E68.filletArc", {"start": v(-104.6, 9.15) * mm, "mid": v(-104.94, 9.33) * mm, "end": v(-105.31, 9.2) * mm});
            skPoint(sketch, "E69.visualSharp", {"position": v(-105.91, 8.65) * mm});
            skArc(sketch, "E69.filletArc", {"start": v(-105.54, 9) * mm, "mid": v(-105.7, 8.65) * mm, "end": v(-105.56, 8.28) * mm});
            skLineSegment(sketch, "E70.1.0", {"start": v(-96.12, -1.34) * mm, "end": v(-102.8, 10.37) * mm});
            skLineSegment(sketch, "E70.1.1", {"start": v(-96.12, -1.34) * mm, "end": v(-103.89, 9.68) * mm});
            skArc(sketch, "E70.1.2", {"start": v(-102.8, 10.37) * mm, "mid": v(-103.1, 10.6) * mm, "end": v(-103.5, 10.55) * mm});
            skEllipticalArc(sketch, "E70.1.3", {});
            skArc(sketch, "E70.1.4", {"start": v(-103.75, 10.38) * mm, "mid": v(-103.97, 10.06) * mm, "end": v(-103.89, 9.68) * mm});
            skLineSegment(sketch, "E70.2.0", {"start": v(-96.12, -1.34) * mm, "end": v(-100.83, 11.3) * mm});
            skLineSegment(sketch, "E70.2.1", {"start": v(-96.12, -1.34) * mm, "end": v(-102.01, 10.78) * mm});
            skArc(sketch, "E70.2.2", {"start": v(-100.83, 11.3) * mm, "mid": v(-101.1, 11.58) * mm, "end": v(-101.49, 11.58) * mm});
            skEllipticalArc(sketch, "E70.2.3", {});
            skArc(sketch, "E70.2.4", {"start": v(-101.77, 11.46) * mm, "mid": v(-102.03, 11.17) * mm, "end": v(-102.01, 10.78) * mm});
            skLineSegment(sketch, "E70.3.0", {"start": v(-96.12, -1.34) * mm, "end": v(-98.73, 11.88) * mm});
            skLineSegment(sketch, "E70.3.1", {"start": v(-96.12, -1.34) * mm, "end": v(-99.99, 11.57) * mm});
            skArc(sketch, "E70.3.2", {"start": v(-98.73, 11.88) * mm, "mid": v(-98.95, 12.2) * mm, "end": v(-99.34, 12.27) * mm});
            skEllipticalArc(sketch, "E70.3.3", {});
            skArc(sketch, "E70.3.4", {"start": v(-99.64, 12.2) * mm, "mid": v(-99.94, 11.96) * mm, "end": v(-99.99, 11.57) * mm});
            skLineSegment(sketch, "E70.4.0", {"start": v(-96.12, -1.34) * mm, "end": v(-96.57, 12.13) * mm});
            skLineSegment(sketch, "E70.4.1", {"start": v(-96.12, -1.34) * mm, "end": v(-97.86, 12.03) * mm});
            skArc(sketch, "E70.4.2", {"start": v(-96.57, 12.13) * mm, "mid": v(-96.74, 12.49) * mm, "end": v(-97.1, 12.61) * mm});
            skEllipticalArc(sketch, "E70.4.3", {});
            skArc(sketch, "E70.4.4", {"start": v(-97.41, 12.59) * mm, "mid": v(-97.76, 12.4) * mm, "end": v(-97.86, 12.03) * mm});
            skLineSegment(sketch, "E70.5.0", {"start": v(-96.12, -1.34) * mm, "end": v(-94.4, 12.03) * mm});
            skLineSegment(sketch, "E70.5.1", {"start": v(-96.12, -1.34) * mm, "end": v(-95.69, 12.13) * mm});
            skArc(sketch, "E70.5.2", {"start": v(-94.4, 12.03) * mm, "mid": v(-94.5, 12.4) * mm, "end": v(-94.85, 12.6) * mm});
            skEllipticalArc(sketch, "E70.5.3", {});
            skArc(sketch, "E70.5.4", {"start": v(-95.16, 12.61) * mm, "mid": v(-95.52, 12.49) * mm, "end": v(-95.69, 12.13) * mm});
            skLineSegment(sketch, "E70.6.0", {"start": v(-96.12, -1.34) * mm, "end": v(-92.27, 11.58) * mm});
            skLineSegment(sketch, "E70.6.1", {"start": v(-96.12, -1.34) * mm, "end": v(-93.53, 11.89) * mm});
            skArc(sketch, "E70.6.2", {"start": v(-92.27, 11.58) * mm, "mid": v(-92.32, 11.97) * mm, "end": v(-92.63, 12.2) * mm});
            skEllipticalArc(sketch, "E70.6.3", {});
            skArc(sketch, "E70.6.4", {"start": v(-92.92, 12.28) * mm, "mid": v(-93.3, 12.21) * mm, "end": v(-93.53, 11.89) * mm});
            skLineSegment(sketch, "E70.7.0", {"start": v(-96.12, -1.34) * mm, "end": v(-90.24, 10.8) * mm});
            skLineSegment(sketch, "E70.7.1", {"start": v(-96.12, -1.34) * mm, "end": v(-91.43, 11.3) * mm});
            skArc(sketch, "E70.7.2", {"start": v(-90.24, 10.8) * mm, "mid": v(-90.23, 11.18) * mm, "end": v(-90.5, 11.47) * mm});
            skEllipticalArc(sketch, "E70.7.3", {});
            skArc(sketch, "E70.7.4", {"start": v(-90.78, 11.59) * mm, "mid": v(-91.17, 11.58) * mm, "end": v(-91.43, 11.3) * mm});
            skLineSegment(sketch, "E70.8.0", {"start": v(-96.12, -1.34) * mm, "end": v(-88.37, 9.69) * mm});
            skLineSegment(sketch, "E70.8.1", {"start": v(-96.12, -1.34) * mm, "end": v(-89.46, 10.38) * mm});
            skArc(sketch, "E70.8.2", {"start": v(-88.37, 9.69) * mm, "mid": v(-88.29, 10.07) * mm, "end": v(-88.5, 10.4) * mm});
            skEllipticalArc(sketch, "E70.8.3", {});
            skArc(sketch, "E70.8.4", {"start": v(-88.77, 10.56) * mm, "mid": v(-89.15, 10.62) * mm, "end": v(-89.46, 10.38) * mm});
            skLineSegment(sketch, "E70.9.0", {"start": v(-96.12, -1.34) * mm, "end": v(-86.7, 8.3) * mm});
            skLineSegment(sketch, "E70.9.1", {"start": v(-96.12, -1.34) * mm, "end": v(-87.67, 9.15) * mm});
            skArc(sketch, "E70.9.2", {"start": v(-86.7, 8.3) * mm, "mid": v(-86.56, 8.66) * mm, "end": v(-86.72, 9.02) * mm});
            skEllipticalArc(sketch, "E70.9.3", {});
            skArc(sketch, "E70.9.4", {"start": v(-86.95, 9.22) * mm, "mid": v(-87.32, 9.34) * mm, "end": v(-87.67, 9.15) * mm});
            skPoint(sketch, "E71.center", {"position": v(-77.09, -3.64) * mm});
            skLineSegment(sketch, "E71.anchor1", {"start": v(-77.09, -3.64) * mm, "end": v(-77.09, -3.64) * mm});
            skLineSegment(sketch, "E71.anchor2", {"start": v(-77.09, -3.64) * mm, "end": v(-64.03, -3.64) * mm, "construction": true});
            skPoint(sketch, "E72.visualSharp", {"position": v(-86.02, 7.41) * mm});
            skPoint(sketch, "E73.visualSharp", {"position": v(-87.02, 6.48) * mm});
            skLineSegment(sketch, "E74.1.0", {"start": v(-77.09, -3.64) * mm, "end": v(-83.87, 8.25) * mm});
            skLineSegment(sketch, "E74.1.1", {"start": v(-77.09, -3.64) * mm, "end": v(-84.98, 7.54) * mm});
            skArc(sketch, "E74.1.2", {"start": v(-83.87, 8.25) * mm, "mid": v(-84.19, 8.5) * mm, "end": v(-84.58, 8.42) * mm});
            skEllipticalArc(sketch, "E74.1.3", {});
            skArc(sketch, "E74.1.4", {"start": v(-84.85, 8.24) * mm, "mid": v(-85.06, 7.92) * mm, "end": v(-84.98, 7.54) * mm});
            skLineSegment(sketch, "E74.2.0", {"start": v(-77.09, -3.64) * mm, "end": v(-81.87, 9.19) * mm});
            skLineSegment(sketch, "E74.2.1", {"start": v(-77.09, -3.64) * mm, "end": v(-83.07, 8.67) * mm});
            skArc(sketch, "E74.2.2", {"start": v(-81.87, 9.19) * mm, "mid": v(-82.14, 9.47) * mm, "end": v(-82.54, 9.47) * mm});
            skEllipticalArc(sketch, "E74.2.3", {});
            skArc(sketch, "E74.2.4", {"start": v(-82.84, 9.34) * mm, "mid": v(-83.1, 9.05) * mm, "end": v(-83.07, 8.67) * mm});
            skLineSegment(sketch, "E74.3.0", {"start": v(-77.09, -3.64) * mm, "end": v(-79.74, 9.79) * mm});
            skLineSegment(sketch, "E74.3.1", {"start": v(-77.09, -3.64) * mm, "end": v(-81.02, 9.47) * mm});
            skArc(sketch, "E74.3.2", {"start": v(-79.74, 9.79) * mm, "mid": v(-79.97, 10.12) * mm, "end": v(-80.36, 10.18) * mm});
            skEllipticalArc(sketch, "E74.3.3", {});
            skArc(sketch, "E74.3.4", {"start": v(-80.67, 10.1) * mm, "mid": v(-80.97, 9.85) * mm, "end": v(-81.02, 9.47) * mm});
            skLineSegment(sketch, "E74.4.0", {"start": v(-77.09, -3.64) * mm, "end": v(-77.55, 10.04) * mm});
            skLineSegment(sketch, "E74.4.1", {"start": v(-77.09, -3.64) * mm, "end": v(-78.86, 9.93) * mm});
            skArc(sketch, "E74.4.2", {"start": v(-77.55, 10.04) * mm, "mid": v(-77.71, 10.4) * mm, "end": v(-78.1, 10.52) * mm});
            skEllipticalArc(sketch, "E74.4.3", {});
            skArc(sketch, "E74.4.4", {"start": v(-78.42, 10.49) * mm, "mid": v(-78.75, 10.3) * mm, "end": v(-78.86, 9.93) * mm});
            skLineSegment(sketch, "E74.5.0", {"start": v(-77.09, -3.64) * mm, "end": v(-75.34, 9.94) * mm});
            skLineSegment(sketch, "E74.5.1", {"start": v(-77.09, -3.64) * mm, "end": v(-76.65, 10.04) * mm});
            skArc(sketch, "E74.5.2", {"start": v(-75.34, 9.94) * mm, "mid": v(-75.45, 10.32) * mm, "end": v(-75.8, 10.5) * mm});
            skEllipticalArc(sketch, "E74.5.3", {});
            skArc(sketch, "E74.5.4", {"start": v(-76.12, 10.52) * mm, "mid": v(-76.49, 10.39) * mm, "end": v(-76.65, 10.04) * mm});
            skLineSegment(sketch, "E74.6.0", {"start": v(-77.09, -3.64) * mm, "end": v(-73.18, 9.48) * mm});
            skLineSegment(sketch, "E74.6.1", {"start": v(-77.09, -3.64) * mm, "end": v(-74.45, 9.79) * mm});
            skArc(sketch, "E74.6.2", {"start": v(-73.18, 9.48) * mm, "mid": v(-73.22, 9.87) * mm, "end": v(-73.54, 10.1) * mm});
            skEllipticalArc(sketch, "E74.6.3", {});
            skArc(sketch, "E74.6.4", {"start": v(-73.86, 10.18) * mm, "mid": v(-74.24, 10.1) * mm, "end": v(-74.45, 9.79) * mm});
            skLineSegment(sketch, "E74.7.0", {"start": v(-77.09, -3.64) * mm, "end": v(-71.12, 8.68) * mm});
            skLineSegment(sketch, "E74.7.1", {"start": v(-77.09, -3.64) * mm, "end": v(-72.33, 9.19) * mm});
            skArc(sketch, "E74.7.2", {"start": v(-71.12, 8.68) * mm, "mid": v(-71.1, 9.07) * mm, "end": v(-71.37, 9.36) * mm});
            skEllipticalArc(sketch, "E74.7.3", {});
            skArc(sketch, "E74.7.4", {"start": v(-71.68, 9.48) * mm, "mid": v(-72.06, 9.47) * mm, "end": v(-72.33, 9.19) * mm});
            skLineSegment(sketch, "E74.8.0", {"start": v(-77.09, -3.64) * mm, "end": v(-69.21, 7.56) * mm});
            skLineSegment(sketch, "E74.8.1", {"start": v(-77.09, -3.64) * mm, "end": v(-70.33, 8.25) * mm});
            skArc(sketch, "E74.8.2", {"start": v(-69.21, 7.56) * mm, "mid": v(-69.13, 7.94) * mm, "end": v(-69.36, 8.27) * mm});
            skEllipticalArc(sketch, "E74.8.3", {});
            skArc(sketch, "E74.8.4", {"start": v(-69.64, 8.44) * mm, "mid": v(-70.02, 8.5) * mm, "end": v(-70.33, 8.25) * mm});
            skPoint(sketch, "E75.1.0.0", {"position": v(-57.78, -3.64) * mm});
            skLineSegment(sketch, "E75.1.0.1", {"start": v(-57.78, -3.64) * mm, "end": v(-51.81, 8.68) * mm});
            skLineSegment(sketch, "E75.1.0.2", {"start": v(-57.78, -3.64) * mm, "end": v(-62.56, 9.19) * mm});
            skLineSegment(sketch, "E75.1.0.3", {"start": v(-57.78, -3.64) * mm, "end": v(-57.34, 10.04) * mm});
            skLineSegment(sketch, "E75.1.0.4", {"start": v(-57.78, -3.64) * mm, "end": v(-51.02, 8.25) * mm});
            skLineSegment(sketch, "E75.1.0.5", {"start": v(-57.78, -3.64) * mm, "end": v(-55.15, 9.79) * mm});
            skLineSegment(sketch, "E75.1.0.6", {"start": v(-57.78, -3.64) * mm, "end": v(-49.9, 7.56) * mm});
            skLineSegment(sketch, "E75.1.0.7", {"start": v(-57.78, -3.64) * mm, "end": v(-58.24, 10.04) * mm});
            skLineSegment(sketch, "E75.1.0.8", {"start": v(-57.78, -3.64) * mm, "end": v(-53.02, 9.19) * mm});
            skLineSegment(sketch, "E75.1.0.9", {"start": v(-57.78, -3.64) * mm, "end": v(-65.67, 7.54) * mm});
            skLineSegment(sketch, "E75.1.0.10", {"start": v(-57.78, -3.64) * mm, "end": v(-53.87, 9.48) * mm});
            skLineSegment(sketch, "E75.1.0.11", {"start": v(-57.78, -3.64) * mm, "end": v(-60.44, 9.79) * mm});
            skLineSegment(sketch, "E75.1.0.12", {"start": v(-57.78, -3.64) * mm, "end": v(-61.7, 9.47) * mm});
            skLineSegment(sketch, "E75.1.0.13", {"start": v(-57.78, -3.64) * mm, "end": v(-56.03, 9.94) * mm});
            skLineSegment(sketch, "E75.1.0.14", {"start": v(-57.78, -3.64) * mm, "end": v(-63.77, 8.67) * mm});
            skLineSegment(sketch, "E75.1.0.15", {"start": v(-57.78, -3.64) * mm, "end": v(-59.55, 9.93) * mm});
            skLineSegment(sketch, "E75.1.0.16", {"start": v(-57.78, -3.64) * mm, "end": v(-64.56, 8.25) * mm});
            skPoint(sketch, "E75.1.0.17", {"position": v(-57.78, -3.64) * mm});
            skArc(sketch, "E75.1.0.18", {"start": v(-52.37, 9.48) * mm, "mid": v(-52.76, 9.47) * mm, "end": v(-53.02, 9.19) * mm});
            skEllipticalArc(sketch, "E75.1.0.19", {});
            skArc(sketch, "E75.1.0.20", {"start": v(-65.54, 8.24) * mm, "mid": v(-65.75, 7.92) * mm, "end": v(-65.67, 7.54) * mm});
            skEllipticalArc(sketch, "E75.1.0.21", {});
            skArc(sketch, "E75.1.0.22", {"start": v(-64.56, 8.25) * mm, "mid": v(-64.88, 8.5) * mm, "end": v(-65.27, 8.42) * mm});
            skArc(sketch, "E75.1.0.23", {"start": v(-51.81, 8.68) * mm, "mid": v(-51.8, 9.07) * mm, "end": v(-52.07, 9.36) * mm});
            skArc(sketch, "E75.1.0.24", {"start": v(-60.44, 9.79) * mm, "mid": v(-60.66, 10.12) * mm, "end": v(-61.05, 10.18) * mm});
            skArc(sketch, "E75.1.0.25", {"start": v(-62.56, 9.19) * mm, "mid": v(-62.84, 9.47) * mm, "end": v(-63.23, 9.47) * mm});
            skArc(sketch, "E75.1.0.26", {"start": v(-53.87, 9.48) * mm, "mid": v(-53.92, 9.87) * mm, "end": v(-54.23, 10.1) * mm});
            skEllipticalArc(sketch, "E75.1.0.27", {});
            skEllipticalArc(sketch, "E75.1.0.28", {});
            skArc(sketch, "E75.1.0.29", {"start": v(-54.55, 10.18) * mm, "mid": v(-54.93, 10.1) * mm, "end": v(-55.15, 9.79) * mm});
            skArc(sketch, "E75.1.0.30", {"start": v(-59.1, 10.49) * mm, "mid": v(-59.45, 10.3) * mm, "end": v(-59.55, 9.93) * mm});
            skArc(sketch, "E75.1.0.31", {"start": v(-56.03, 9.94) * mm, "mid": v(-56.14, 10.32) * mm, "end": v(-56.5, 10.5) * mm});
            skEllipticalArc(sketch, "E75.1.0.32", {});
            skArc(sketch, "E75.1.0.33", {"start": v(-61.37, 10.1) * mm, "mid": v(-61.67, 9.85) * mm, "end": v(-61.7, 9.47) * mm});
            skEllipticalArc(sketch, "E75.1.0.34", {});
            skArc(sketch, "E75.1.0.35", {"start": v(-50.33, 8.44) * mm, "mid": v(-50.71, 8.5) * mm, "end": v(-51.02, 8.25) * mm});
            skArc(sketch, "E75.1.0.36", {"start": v(-56.82, 10.52) * mm, "mid": v(-57.18, 10.39) * mm, "end": v(-57.34, 10.04) * mm});
            skArc(sketch, "E75.1.0.37", {"start": v(-58.24, 10.04) * mm, "mid": v(-58.4, 10.4) * mm, "end": v(-58.78, 10.52) * mm});
            skArc(sketch, "E75.1.0.38", {"start": v(-49.9, 7.56) * mm, "mid": v(-49.82, 7.94) * mm, "end": v(-50.05, 8.27) * mm});
            skArc(sketch, "E75.1.0.39", {"start": v(-63.53, 9.34) * mm, "mid": v(-63.79, 9.05) * mm, "end": v(-63.77, 8.67) * mm});
            skEllipticalArc(sketch, "E75.1.0.40", {});
            skPoint(sketch, "E75.2.0.0", {"position": v(-38.48, -3.64) * mm});
            skLineSegment(sketch, "E75.2.0.1", {"start": v(-38.48, -3.64) * mm, "end": v(-32.5, 8.68) * mm});
            skLineSegment(sketch, "E75.2.0.2", {"start": v(-38.48, -3.64) * mm, "end": v(-43.26, 9.19) * mm});
            skLineSegment(sketch, "E75.2.0.3", {"start": v(-38.48, -3.64) * mm, "end": v(-38.04, 10.04) * mm});
            skLineSegment(sketch, "E75.2.0.4", {"start": v(-38.48, -3.64) * mm, "end": v(-31.71, 8.25) * mm});
            skLineSegment(sketch, "E75.2.0.5", {"start": v(-38.48, -3.64) * mm, "end": v(-35.84, 9.79) * mm});
            skLineSegment(sketch, "E75.2.0.6", {"start": v(-38.48, -3.64) * mm, "end": v(-30.6, 7.56) * mm});
            skLineSegment(sketch, "E75.2.0.7", {"start": v(-38.48, -3.64) * mm, "end": v(-38.93, 10.04) * mm});
            skLineSegment(sketch, "E75.2.0.8", {"start": v(-38.48, -3.64) * mm, "end": v(-33.71, 9.19) * mm});
            skLineSegment(sketch, "E75.2.0.9", {"start": v(-38.48, -3.64) * mm, "end": v(-46.36, 7.54) * mm});
            skLineSegment(sketch, "E75.2.0.10", {"start": v(-38.48, -3.64) * mm, "end": v(-34.56, 9.48) * mm});
            skLineSegment(sketch, "E75.2.0.11", {"start": v(-38.48, -3.64) * mm, "end": v(-41.13, 9.79) * mm});
            skLineSegment(sketch, "E75.2.0.12", {"start": v(-38.48, -3.64) * mm, "end": v(-42.4, 9.47) * mm});
            skLineSegment(sketch, "E75.2.0.13", {"start": v(-38.48, -3.64) * mm, "end": v(-36.73, 9.94) * mm});
            skLineSegment(sketch, "E75.2.0.14", {"start": v(-38.48, -3.64) * mm, "end": v(-44.46, 8.67) * mm});
            skLineSegment(sketch, "E75.2.0.15", {"start": v(-38.48, -3.64) * mm, "end": v(-40.24, 9.93) * mm});
            skLineSegment(sketch, "E75.2.0.16", {"start": v(-38.48, -3.64) * mm, "end": v(-45.26, 8.25) * mm});
            skPoint(sketch, "E75.2.0.17", {"position": v(-38.48, -3.64) * mm});
            skArc(sketch, "E75.2.0.18", {"start": v(-33.06, 9.48) * mm, "mid": v(-33.45, 9.47) * mm, "end": v(-33.71, 9.19) * mm});
            skEllipticalArc(sketch, "E75.2.0.19", {});
            skArc(sketch, "E75.2.0.20", {"start": v(-46.24, 8.24) * mm, "mid": v(-46.45, 7.92) * mm, "end": v(-46.36, 7.54) * mm});
            skEllipticalArc(sketch, "E75.2.0.21", {});
            skArc(sketch, "E75.2.0.22", {"start": v(-45.26, 8.25) * mm, "mid": v(-45.57, 8.5) * mm, "end": v(-45.96, 8.42) * mm});
            skArc(sketch, "E75.2.0.23", {"start": v(-32.5, 8.68) * mm, "mid": v(-32.49, 9.07) * mm, "end": v(-32.76, 9.36) * mm});
            skArc(sketch, "E75.2.0.24", {"start": v(-41.13, 9.79) * mm, "mid": v(-41.35, 10.12) * mm, "end": v(-41.74, 10.18) * mm});
            skArc(sketch, "E75.2.0.25", {"start": v(-43.26, 9.19) * mm, "mid": v(-43.53, 9.47) * mm, "end": v(-43.92, 9.47) * mm});
            skArc(sketch, "E75.2.0.26", {"start": v(-34.56, 9.48) * mm, "mid": v(-34.6, 9.87) * mm, "end": v(-34.93, 10.1) * mm});
            skEllipticalArc(sketch, "E75.2.0.27", {});
            skEllipticalArc(sketch, "E75.2.0.28", {});
            skArc(sketch, "E75.2.0.29", {"start": v(-35.25, 10.18) * mm, "mid": v(-35.63, 10.1) * mm, "end": v(-35.84, 9.79) * mm});
            skArc(sketch, "E75.2.0.30", {"start": v(-39.8, 10.49) * mm, "mid": v(-40.14, 10.3) * mm, "end": v(-40.24, 9.93) * mm});
            skArc(sketch, "E75.2.0.31", {"start": v(-36.73, 9.94) * mm, "mid": v(-36.83, 10.32) * mm, "end": v(-37.19, 10.5) * mm});
            skEllipticalArc(sketch, "E75.2.0.32", {});
            skArc(sketch, "E75.2.0.33", {"start": v(-42.06, 10.1) * mm, "mid": v(-42.36, 9.85) * mm, "end": v(-42.4, 9.47) * mm});
            skEllipticalArc(sketch, "E75.2.0.34", {});
            skArc(sketch, "E75.2.0.35", {"start": v(-31.02, 8.44) * mm, "mid": v(-31.4, 8.5) * mm, "end": v(-31.71, 8.25) * mm});
            skArc(sketch, "E75.2.0.36", {"start": v(-37.51, 10.52) * mm, "mid": v(-37.87, 10.39) * mm, "end": v(-38.04, 10.04) * mm});
            skArc(sketch, "E75.2.0.37", {"start": v(-38.93, 10.04) * mm, "mid": v(-39.1, 10.4) * mm, "end": v(-39.48, 10.52) * mm});
            skArc(sketch, "E75.2.0.38", {"start": v(-30.6, 7.56) * mm, "mid": v(-30.52, 7.94) * mm, "end": v(-30.74, 8.27) * mm});
            skArc(sketch, "E75.2.0.39", {"start": v(-44.22, 9.34) * mm, "mid": v(-44.48, 9.05) * mm, "end": v(-44.46, 8.67) * mm});
            skEllipticalArc(sketch, "E75.2.0.40", {});
            skLineSegment(sketch, "E75.direction1", {"start": v(-77.09, -3.64) * mm, "end": v(-57.78, -3.64) * mm, "construction": true});
            skLineSegment(sketch, "E76", {"start": v(-59.1, 10.49) * mm, "end": v(-58.78, 10.52) * mm});
            skLineSegment(sketch, "E77", {"start": v(-39.8, 10.49) * mm, "end": v(-39.48, 10.52) * mm});
            const initialGuessF17  = {"E64.0": [-0.09612256447526175, -0.0013360511020651194, 0, 1, 0.014, 0.013965054578359462, 0.7180546312957505, 0.7398930087092236], "E70.1.3": [-0.09612256447526175, -0.0013360511020651198, 0.16086763624185027, 0.9869759893786473, 0.014, 0.013965054578359462, 0.718054631295751, 0.7398930087092235], "E70.2.3": [-0.09612256447526175, -0.001336051102065118, 0.317544988877609, 0.9482432072199195, 0.014, 0.013965054578359462, 0.718054631295751, 0.7398930087092231], "E70.3.3": [-0.09612256447526175, -0.001336051102065118, 0.4659509228975692, 0.8848105658562762, 0.014, 0.013965054578359462, 0.718054631295751, 0.7398930087092234], "E70.4.3": [-0.09612256447526175, -0.001336051102065118, 0.6022197573798352, 0.7983303600774383, 0.014, 0.01396505457835946, 0.7180546312957504, 0.739893008709224], "E70.5.3": [-0.09612256447526175, -0.0013360511020651194, 0.722801958829093, 0.6910552281206084, 0.014, 0.013965054578359462, 0.718054631295748, 0.7398930087092209], "E70.6.3": [-0.09612256447526175, -0.0013360511020651194, 0.8245565995005028, 0.5657794749018097, 0.014, 0.013965054578359462, 0.7180546312957475, 0.7398930087092203], "E70.7.3": [-0.09612256447526175, -0.0013360511020651194, 0.904833172352311, 0.4257662859020819, 0.014, 0.013965054578359462, 0.718054631295746, 0.7398930087092198], "E70.8.3": [-0.09612256447526175, -0.0013360511020651194, 0.9615406315095817, 0.2746627276427487, 0.014, 0.013965054578359462, 0.7180546312957461, 0.7398930087092197], "E70.9.3": [-0.09612256447526175, -0.0013360511020651194, 0.9932018598715668, 0.11640474881919785, 0.014, 0.013965054578359462, 0.7180546312957454, 0.7398930087092193], "E74.1.3": [-0.07708931073374041, -0.003644061778911401, 0.160867636241799, 0.9869759893786557, 0.014323932052886448, 0.014046620573596253, 0.7265398216981758, 0.7495844923670351], "E74.2.3": [-0.07708931075018732, -0.0036440627026220612, 0.3175448508741828, 0.9482432534341034, 0.014323932052886448, 0.014046620573596253, 0.7265398216981759, 0.7495844923670342], "E74.3.3": [-0.07708931091501504, -0.0036440636116565443, 0.4659506653542021, 0.8848107014813827, 0.014323932052886448, 0.014046620573596253, 0.726539821698176, 0.749584492367036], "E74.4.3": [-0.07708931122393015, -0.003644064482336354, 0.602219408822693, 0.7983306230110719, 0.014323932052886448, 0.014046620573596253, 0.7265398216981779, 0.7495844923670363], "E74.5.3": [-0.07708931166888604, -0.0036440652919820377, 0.7228015565357182, 0.6910556488948941, 0.014323932052886448, 0.014046620573596253, 0.7265398216981772, 0.7495844923670363], "E74.6.3": [-0.07708931223829249, -0.003644066019503976, 0.8245561877942955, 0.5657800749143952, 0.014323932052886448, 0.014046620573596253, 0.7265398216981775, 0.749584492367036], "E74.7.3": [-0.07708931291731765, -0.0036440666459516824, 0.9048328005664158, 0.4257670760159087, 0.014323932052886448, 0.014046620573596253, 0.7265398216981768, 0.7495844923670354], "E74.8.3": [-0.07708931368827424, -0.003644067155007466, 0.9615403516961704, 0.27466370721303013, 0.014323932052886448, 0.014046620573596253, 0.7265398216981767, 0.7495844923670362], "E75.1.0.19": [-0.057782832917317645, -0.0036440666459516824, 0.904832800566416, 0.4257670760159088, 0.014323932052886448, 0.014046620573596253, 0.7265398216981768, 0.7495844923670354], "E75.1.0.21": [-0.05778283073374041, -0.003644061778911401, 0.160867636241799, 0.9869759893786557, 0.014323932052886448, 0.014046620573596253, 0.7265398216981755, 0.7495844923670351], "E75.1.0.27": [-0.05778283166888604, -0.0036440652919820377, 0.7228015565357182, 0.6910556488948941, 0.014323932052886448, 0.014046620573596253, 0.7265398216981772, 0.7495844923670363], "E75.1.0.28": [-0.05778283091501504, -0.0036440636116565443, 0.4659506653542021, 0.8848107014813827, 0.014323932052886448, 0.014046620573596253, 0.726539821698176, 0.749584492367036], "E75.1.0.32": [-0.057782833688274235, -0.003644067155007466, 0.9615403516961704, 0.27466370721303013, 0.014323932052886448, 0.014046620573596253, 0.7265398216981767, 0.7495844923670362], "E75.1.0.34": [-0.05778283075018732, -0.0036440627026220612, 0.3175448508741828, 0.9482432534341034, 0.014323932052886448, 0.014046620573596253, 0.7265398216981759, 0.7495844923670342], "E75.1.0.40": [-0.05778283223829249, -0.003644066019503976, 0.8245561877942955, 0.5657800749143952, 0.014323932052886448, 0.014046620573596253, 0.7265398216981775, 0.749584492367036], "E75.2.0.19": [-0.038476352917317644, -0.0036440666459516824, 0.904832800566416, 0.4257670760159088, 0.014323932052886448, 0.014046620573596253, 0.7265398216981768, 0.7495844923670354], "E75.2.0.21": [-0.03847635073374041, -0.003644061778911401, 0.160867636241799, 0.9869759893786557, 0.014323932052886448, 0.014046620573596253, 0.7265398216981755, 0.7495844923670351], "E75.2.0.27": [-0.038476351668886036, -0.0036440652919820377, 0.7228015565357182, 0.6910556488948941, 0.014323932052886448, 0.014046620573596253, 0.7265398216981772, 0.7495844923670363], "E75.2.0.28": [-0.03847635091501504, -0.0036440636116565443, 0.4659506653542021, 0.8848107014813827, 0.014323932052886448, 0.014046620573596253, 0.726539821698176, 0.749584492367036], "E75.2.0.32": [-0.038476353688274234, -0.003644067155007466, 0.9615403516961704, 0.27466370721303013, 0.014323932052886448, 0.014046620573596253, 0.7265398216981767, 0.7495844923670362], "E75.2.0.34": [-0.03847635075018732, -0.0036440627026220612, 0.3175448508741828, 0.9482432534341034, 0.014323932052886448, 0.014046620573596253, 0.7265398216981759, 0.7495844923670342], "E75.2.0.40": [-0.03847635223829249, -0.003644066019503976, 0.8245561877942955, 0.5657800749143952, 0.014323932052886448, 0.014046620573596253, 0.7265398216981775, 0.749584492367036]};
            skSetInitialGuess(sketch, initialGuessF17);
            skSolve(sketch);
        }
        {
            var Q0;
            Q0=qSketchRegion(id+"F17",true);
            extrude(context, id + "F18", {"entities" : qUnion([Q0]), "operationType" : NewBodyOperationType.REMOVE, "endBound" : BoundingType.SYMMETRIC, "oppositeDirection" : true, "depth" : 40 * mm});
        }
        {
            var Q0;
            Q0=makeQuery(id+"F1.opExtrude","SWEPT_FACE",FACE,{"disambiguationData":[OSD([sQuery(id+"F0.wireOp",EDGE,"E21.MirrorCS")])]});
            var sketch = newSketch(context, id + "F19", { "sketchPlane" : qUnion([Q0])});
            skLineSegment(sketch, "E78", {"start": v(-182.27, 9.85) * mm, "end": v(-182.27, 5.5) * mm});
            skLineSegment(sketch, "E79", {"start": v(-182.27, 5.5) * mm, "end": v(-221.62, 5.5) * mm});
            skLineSegment(sketch, "E80", {"start": v(-221.62, 5.5) * mm, "end": v(-221.62, 9.85) * mm});
            skLineSegment(sketch, "E81", {"start": v(-221.62, 9.85) * mm, "end": v(-182.27, 9.85) * mm});
            skSolve(sketch);
        }
        {
            var Q0;
            Q0=makeQuery(id+"F19.imprint","IMPRINT",FACE,{"disambiguationData":[TD([[makeQuery(id+"F19.imprint","IMPRINT",EDGE,{"derivedFrom":sQuery(id+"F19.wireOp",EDGE,"E78")}),-1.0]])]});
            extrude(context, id + "F20", {"entities" : qUnion([Q0]), "endBound" : BoundingType.SYMMETRIC, "depth" : 30 * mm});
        }
        {
            var Q0;
            Q0=makeQuery(id+"F1.opExtrude","SWEPT_BODY",BODY,{"disambiguationData":[OSD([sQuery(id+"F0.wireOp",EDGE,"E1"),sQuery(id+"F0.wireOp",EDGE,"E8"),sQuery(id+"F0.wireOp",EDGE,"E9"),sQuery(id+"F0.wireOp",EDGE,"E10"),sQuery(id+"F0.wireOp",EDGE,"E11"),sQuery(id+"F0.wireOp",EDGE,"E12"),sQuery(id+"F0.wireOp",EDGE,"E13"),sQuery(id+"F0.wireOp",EDGE,"E14"),sQuery(id+"F0.wireOp",EDGE,"E15"),sQuery(id+"F0.wireOp",EDGE,"E16.MirrorCS"),sQuery(id+"F0.wireOp",EDGE,"E17.MirrorCS"),sQuery(id+"F0.wireOp",EDGE,"E18.MirrorCS"),sQuery(id+"F0.wireOp",EDGE,"E19.MirrorCS"),sQuery(id+"F0.wireOp",EDGE,"E20.MirrorCS"),sQuery(id+"F0.wireOp",EDGE,"E21.MirrorCS"),sQuery(id+"F0.wireOp",EDGE,"E22.MirrorCS"),sQuery(id+"F0.wireOp",EDGE,"E23.MirrorCS"),sQuery(id+"F0.wireOp",EDGE,"E24.MirrorCS")])]});
            var Q1;
            Q1=makeQuery(id+"F20.opExtrude","SWEPT_BODY",BODY,{"disambiguationData":[OSD([sQuery(id+"F19.wireOp",EDGE,"E78"),sQuery(id+"F19.wireOp",EDGE,"E79"),sQuery(id+"F19.wireOp",EDGE,"E80"),sQuery(id+"F19.wireOp",EDGE,"E81")])]});
            booleanBodies(context, id + "F21", {"operationType" : BooleanOperationType.INTERSECTION, "tools" : qUnion([Q0, Q1]), "keepTools" : true});
        }
        {
            var Q0;
            Q0=makeQuery(id+"F21.opBoolean","INTERSECT",BODY,{"derivedFrom":[makeQuery(id+"F1.opExtrude","SWEPT_BODY",BODY,{"disambiguationData":[OSD([sQuery(id+"F0.wireOp",EDGE,"E1"),sQuery(id+"F0.wireOp",EDGE,"E8"),sQuery(id+"F0.wireOp",EDGE,"E9"),sQuery(id+"F0.wireOp",EDGE,"E10"),sQuery(id+"F0.wireOp",EDGE,"E11"),sQuery(id+"F0.wireOp",EDGE,"E12"),sQuery(id+"F0.wireOp",EDGE,"E13"),sQuery(id+"F0.wireOp",EDGE,"E14"),sQuery(id+"F0.wireOp",EDGE,"E15"),sQuery(id+"F0.wireOp",EDGE,"E16.MirrorCS"),sQuery(id+"F0.wireOp",EDGE,"E17.MirrorCS"),sQuery(id+"F0.wireOp",EDGE,"E18.MirrorCS"),sQuery(id+"F0.wireOp",EDGE,"E19.MirrorCS"),sQuery(id+"F0.wireOp",EDGE,"E20.MirrorCS"),sQuery(id+"F0.wireOp",EDGE,"E21.MirrorCS"),sQuery(id+"F0.wireOp",EDGE,"E22.MirrorCS"),sQuery(id+"F0.wireOp",EDGE,"E23.MirrorCS"),sQuery(id+"F0.wireOp",EDGE,"E24.MirrorCS")])]}),makeQuery(id+"F20.opExtrude","SWEPT_BODY",BODY,{"disambiguationData":[OSD([sQuery(id+"F19.wireOp",EDGE,"E78"),sQuery(id+"F19.wireOp",EDGE,"E79"),sQuery(id+"F19.wireOp",EDGE,"E80"),sQuery(id+"F19.wireOp",EDGE,"E81")])]})]});
            var Q1;
            Q1=makeQuery(id+"F1.opExtrude","SWEPT_BODY",BODY,{"disambiguationData":[OSD([sQuery(id+"F0.wireOp",EDGE,"E1"),sQuery(id+"F0.wireOp",EDGE,"E8"),sQuery(id+"F0.wireOp",EDGE,"E9"),sQuery(id+"F0.wireOp",EDGE,"E10"),sQuery(id+"F0.wireOp",EDGE,"E11"),sQuery(id+"F0.wireOp",EDGE,"E12"),sQuery(id+"F0.wireOp",EDGE,"E13"),sQuery(id+"F0.wireOp",EDGE,"E14"),sQuery(id+"F0.wireOp",EDGE,"E15"),sQuery(id+"F0.wireOp",EDGE,"E16.MirrorCS"),sQuery(id+"F0.wireOp",EDGE,"E17.MirrorCS"),sQuery(id+"F0.wireOp",EDGE,"E18.MirrorCS"),sQuery(id+"F0.wireOp",EDGE,"E19.MirrorCS"),sQuery(id+"F0.wireOp",EDGE,"E20.MirrorCS"),sQuery(id+"F0.wireOp",EDGE,"E21.MirrorCS"),sQuery(id+"F0.wireOp",EDGE,"E22.MirrorCS"),sQuery(id+"F0.wireOp",EDGE,"E23.MirrorCS"),sQuery(id+"F0.wireOp",EDGE,"E24.MirrorCS")])]});
            booleanBodies(context, id + "F22", {"operationType" : BooleanOperationType.SUBTRACTION, "tools" : qUnion([Q0]), "targets" : qUnion([Q1]), "keepTools" : true});
        }
        {
            var Q0;
            Q0=makeQuery(id+"F21.opBoolean","COPY",FACE,{"derivedFrom":makeQuery(id+"F3.boolean.opBoolean","COPY",FACE,{"derivedFrom":makeQuery(id+"F3.opExtrude","SWEPT_FACE",FACE,{"disambiguationData":[OSD([sQuery(id+"F2.wireOp",EDGE,"E44")])]})})});
            var sketch = newSketch(context, id + "F23", { "sketchPlane" : qUnion([Q0])});
            skCircle(sketch, "E82.2.0.1", {"center": v(-215.28, 3.65) * mm, "radius": 0.5 * mm});
            skCircle(sketch, "E82.2.0.2", {"center": v(-212.5, 3.65) * mm, "radius": 0.5 * mm});
            skCircle(sketch, "E82.2.0.3", {"center": v(-209.71, 3.65) * mm, "radius": 0.5 * mm});
            skCircle(sketch, "E82.2.0.4", {"center": v(-206.93, 3.65) * mm, "radius": 0.5 * mm});
            skCircle(sketch, "E82.2.0.5", {"center": v(-204.15, 3.65) * mm, "radius": 0.5 * mm});
            skCircle(sketch, "E82.2.0.6", {"center": v(-201.36, 3.65) * mm, "radius": 0.5 * mm});
            skCircle(sketch, "E82.2.0.7", {"center": v(-198.58, 3.65) * mm, "radius": 0.5 * mm});
            skCircle(sketch, "E82.2.0.8", {"center": v(-195.8, 3.65) * mm, "radius": 0.5 * mm});
            skCircle(sketch, "E82.2.0.9", {"center": v(-193.01, 3.65) * mm, "radius": 0.5 * mm});
            skCircle(sketch, "E82.2.0.10", {"center": v(-190.23, 3.65) * mm, "radius": 0.5 * mm});
            skCircle(sketch, "E82.2.0.11", {"center": v(-187.45, 3.65) * mm, "radius": 0.5 * mm});
            skCircle(sketch, "E82.3.0.0", {"center": v(-218.08, 1.23) * mm, "radius": 0.5 * mm});
            skCircle(sketch, "E82.3.0.1", {"center": v(-215.3, 1.23) * mm, "radius": 0.5 * mm});
            skCircle(sketch, "E82.3.0.2", {"center": v(-212.51, 1.23) * mm, "radius": 0.5 * mm});
            skCircle(sketch, "E82.3.0.3", {"center": v(-209.73, 1.23) * mm, "radius": 0.5 * mm});
            skCircle(sketch, "E82.3.0.4", {"center": v(-206.94, 1.23) * mm, "radius": 0.5 * mm});
            skCircle(sketch, "E82.3.0.5", {"center": v(-204.16, 1.23) * mm, "radius": 0.5 * mm});
            skCircle(sketch, "E82.3.0.6", {"center": v(-201.38, 1.23) * mm, "radius": 0.5 * mm});
            skCircle(sketch, "E82.3.0.7", {"center": v(-198.6, 1.23) * mm, "radius": 0.5 * mm});
            skCircle(sketch, "E82.3.0.8", {"center": v(-195.81, 1.23) * mm, "radius": 0.5 * mm});
            skCircle(sketch, "E82.3.0.9", {"center": v(-193.03, 1.23) * mm, "radius": 0.5 * mm});
            skCircle(sketch, "E82.3.0.10", {"center": v(-190.25, 1.23) * mm, "radius": 0.5 * mm});
            skCircle(sketch, "E82.3.0.11", {"center": v(-187.46, 1.23) * mm, "radius": 0.5 * mm});
            skCircle(sketch, "E82.4.0.0", {"center": v(-218.1, -1.2) * mm, "radius": 0.5 * mm});
            skCircle(sketch, "E82.4.0.1", {"center": v(-215.3, -1.2) * mm, "radius": 0.5 * mm});
            skCircle(sketch, "E82.4.0.2", {"center": v(-212.53, -1.2) * mm, "radius": 0.5 * mm});
            skCircle(sketch, "E82.4.0.3", {"center": v(-209.74, -1.2) * mm, "radius": 0.5 * mm});
            skCircle(sketch, "E82.4.0.4", {"center": v(-206.96, -1.2) * mm, "radius": 0.5 * mm});
            skCircle(sketch, "E82.4.0.5", {"center": v(-204.18, -1.2) * mm, "radius": 0.5 * mm});
            skCircle(sketch, "E82.4.0.6", {"center": v(-201.4, -1.2) * mm, "radius": 0.5 * mm});
            skCircle(sketch, "E82.4.0.7", {"center": v(-198.61, -1.2) * mm, "radius": 0.5 * mm});
            skCircle(sketch, "E82.4.0.8", {"center": v(-195.83, -1.2) * mm, "radius": 0.5 * mm});
            skCircle(sketch, "E82.4.0.9", {"center": v(-193.04, -1.2) * mm, "radius": 0.5 * mm});
            skCircle(sketch, "E82.4.0.10", {"center": v(-190.26, -1.2) * mm, "radius": 0.5 * mm});
            skCircle(sketch, "E82.4.0.11", {"center": v(-187.48, -1.2) * mm, "radius": 0.5 * mm});
            skCircle(sketch, "E82.5.0.1", {"center": v(-215.33, -3.62) * mm, "radius": 0.5 * mm});
            skCircle(sketch, "E82.5.0.2", {"center": v(-212.54, -3.62) * mm, "radius": 0.5 * mm});
            skCircle(sketch, "E82.5.0.3", {"center": v(-209.76, -3.62) * mm, "radius": 0.5 * mm});
            skCircle(sketch, "E82.5.0.4", {"center": v(-206.98, -3.62) * mm, "radius": 0.5 * mm});
            skCircle(sketch, "E82.5.0.5", {"center": v(-204.2, -3.62) * mm, "radius": 0.5 * mm});
            skCircle(sketch, "E82.5.0.6", {"center": v(-201.41, -3.62) * mm, "radius": 0.5 * mm});
            skCircle(sketch, "E82.5.0.7", {"center": v(-198.63, -3.62) * mm, "radius": 0.5 * mm});
            skCircle(sketch, "E82.5.0.8", {"center": v(-195.84, -3.62) * mm, "radius": 0.5 * mm});
            skCircle(sketch, "E82.5.0.9", {"center": v(-193.06, -3.62) * mm, "radius": 0.5 * mm});
            skCircle(sketch, "E82.5.0.10", {"center": v(-190.28, -3.62) * mm, "radius": 0.5 * mm});
            skCircle(sketch, "E82.5.0.11", {"center": v(-187.5, -3.62) * mm, "radius": 0.5 * mm});
            skCircle(sketch, "E83", {"center": v(-199.98, 5.12) * mm, "radius": 0.53 * mm});
            skCircle(sketch, "E84", {"center": v(-197.32, 5.26) * mm, "radius": 0.53 * mm});
            skCircle(sketch, "E85", {"center": v(-194.56, 5.64) * mm, "radius": 0.52 * mm});
            skCircle(sketch, "E86", {"center": v(-192.15, 5.67) * mm, "radius": 0.52 * mm});
            skCircle(sketch, "E87", {"center": v(-189.5, 5.2) * mm, "radius": 0.53 * mm});
            skCircle(sketch, "E88", {"center": v(-217.48, 3.14) * mm, "radius": 0.5 * mm});
            skLineSegment(sketch, "E89", {"start": v(-185.17, 0) * mm, "end": v(-221.81, 0.11) * mm, "construction": true});
            skCircle(sketch, "E90.MirrorC", {"center": v(-189.53, -5.17) * mm, "radius": 0.53 * mm});
            skCircle(sketch, "E91.MirrorC", {"center": v(-192.18, -5.63) * mm, "radius": 0.52 * mm});
            skCircle(sketch, "E92.MirrorC", {"center": v(-194.6, -5.58) * mm, "radius": 0.52 * mm});
            skCircle(sketch, "E93.MirrorC", {"center": v(-197.35, -5.19) * mm, "radius": 0.53 * mm});
            skCircle(sketch, "E94.MirrorC", {"center": v(-200, -5.03) * mm, "radius": 0.53 * mm});
            skCircle(sketch, "E95.MirrorC", {"center": v(-217.5, -2.94) * mm, "radius": 0.5 * mm});
            skCircle(sketch, "E96", {"center": v(-213.9, 2.44) * mm, "radius": 0.5 * mm});
            skLineSegment(sketch, "E97", {"start": v(-215.28, 3.65) * mm, "end": v(-212.51, 1.23) * mm, "construction": true});
            skLineSegment(sketch, "E98", {"start": v(-215.3, 1.23) * mm, "end": v(-212.5, 3.65) * mm, "construction": true});
            skCircle(sketch, "E99.1.0.0", {"center": v(-211.1, 2.44) * mm, "radius": 0.5 * mm});
            skCircle(sketch, "E99.2.0.0", {"center": v(-208.3, 2.44) * mm, "radius": 0.5 * mm});
            skCircle(sketch, "E99.3.0.0", {"center": v(-205.5, 2.44) * mm, "radius": 0.5 * mm});
            skCircle(sketch, "E99.4.0.0", {"center": v(-202.7, 2.44) * mm, "radius": 0.5 * mm});
            skCircle(sketch, "E99.5.0.0", {"center": v(-199.9, 2.44) * mm, "radius": 0.5 * mm});
            skCircle(sketch, "E99.6.0.0", {"center": v(-197.1, 2.44) * mm, "radius": 0.5 * mm});
            skCircle(sketch, "E99.7.0.0", {"center": v(-194.3, 2.44) * mm, "radius": 0.5 * mm});
            skCircle(sketch, "E99.8.0.0", {"center": v(-191.5, 2.44) * mm, "radius": 0.5 * mm});
            skCircle(sketch, "E99.9.0.0", {"center": v(-188.7, 2.44) * mm, "radius": 0.5 * mm});
            skCircle(sketch, "E99.10.0.0", {"center": v(-185.9, 2.44) * mm, "radius": 0.5 * mm});
            skLineSegment(sketch, "E99.direction1", {"start": v(-213.9, 2.44) * mm, "end": v(-211.1, 2.44) * mm, "construction": true});
            skCircle(sketch, "E100.1.0.0", {"center": v(-213.93, 0.01) * mm, "radius": 0.5 * mm});
            skCircle(sketch, "E100.1.0.1", {"center": v(-211.13, 0.01) * mm, "radius": 0.5 * mm});
            skCircle(sketch, "E100.1.0.2", {"center": v(-208.34, 0.01) * mm, "radius": 0.5 * mm});
            skCircle(sketch, "E100.1.0.3", {"center": v(-205.54, 0.01) * mm, "radius": 0.5 * mm});
            skCircle(sketch, "E100.1.0.4", {"center": v(-202.74, 0.01) * mm, "radius": 0.5 * mm});
            skCircle(sketch, "E100.1.0.5", {"center": v(-199.94, 0.01) * mm, "radius": 0.5 * mm});
            skCircle(sketch, "E100.1.0.6", {"center": v(-197.14, 0.01) * mm, "radius": 0.5 * mm});
            skCircle(sketch, "E100.1.0.7", {"center": v(-194.34, 0.01) * mm, "radius": 0.5 * mm});
            skCircle(sketch, "E100.1.0.8", {"center": v(-191.54, 0.01) * mm, "radius": 0.5 * mm});
            skCircle(sketch, "E100.1.0.9", {"center": v(-188.74, 0.01) * mm, "radius": 0.5 * mm});
            skCircle(sketch, "E100.1.0.10", {"center": v(-185.95, 0.01) * mm, "radius": 0.5 * mm});
            skCircle(sketch, "E100.2.0.0", {"center": v(-213.97, -2.42) * mm, "radius": 0.5 * mm});
            skCircle(sketch, "E100.2.0.1", {"center": v(-211.17, -2.42) * mm, "radius": 0.5 * mm});
            skCircle(sketch, "E100.2.0.2", {"center": v(-208.37, -2.42) * mm, "radius": 0.5 * mm});
            skCircle(sketch, "E100.2.0.3", {"center": v(-205.58, -2.42) * mm, "radius": 0.5 * mm});
            skCircle(sketch, "E100.2.0.4", {"center": v(-202.78, -2.42) * mm, "radius": 0.5 * mm});
            skCircle(sketch, "E100.2.0.5", {"center": v(-199.98, -2.42) * mm, "radius": 0.5 * mm});
            skCircle(sketch, "E100.2.0.6", {"center": v(-197.18, -2.42) * mm, "radius": 0.5 * mm});
            skCircle(sketch, "E100.2.0.7", {"center": v(-194.38, -2.42) * mm, "radius": 0.5 * mm});
            skCircle(sketch, "E100.2.0.8", {"center": v(-191.58, -2.42) * mm, "radius": 0.5 * mm});
            skCircle(sketch, "E100.2.0.9", {"center": v(-188.78, -2.42) * mm, "radius": 0.5 * mm});
            skCircle(sketch, "E100.2.0.10", {"center": v(-185.99, -2.42) * mm, "radius": 0.5 * mm});
            skLineSegment(sketch, "E100.direction1", {"start": v(-213.9, 2.44) * mm, "end": v(-213.93, 0.01) * mm, "construction": true});
            skCircle(sketch, "E101", {"center": v(-202.7, 4.67) * mm, "radius": 0.5 * mm});
            skCircle(sketch, "E102", {"center": v(-205.5, 4.47) * mm, "radius": 0.5 * mm});
            skCircle(sketch, "E103", {"center": v(-208.3, 4.47) * mm, "radius": 0.5 * mm});
            skCircle(sketch, "E104", {"center": v(-216.69, 0.1) * mm, "radius": 0.51 * mm});
            skCircle(sketch, "E105", {"center": v(-216.67, 2.07) * mm, "radius": 0.54 * mm});
            skCircle(sketch, "E106", {"center": v(-216.67, -1.73) * mm, "radius": 0.54 * mm});
            skCircle(sketch, "E107.MirrorC", {"center": v(-208.32, -4.33) * mm, "radius": 0.5 * mm});
            skCircle(sketch, "E108.MirrorC", {"center": v(-205.52, -4.35) * mm, "radius": 0.5 * mm});
            skCircle(sketch, "E109.MirrorC", {"center": v(-202.73, -4.56) * mm, "radius": 0.5 * mm});
            skSolve(sketch);
        }
        {
            var Q0;
            Q0=qSketchRegion(id+"F23",true);
            extrude(context, id + "F24", {"entities" : qUnion([Q0]), "operationType" : NewBodyOperationType.ADD, "oppositeDirection" : true, "depth" : 2 * mm});
        }
        {
            var Q0;
            Q0=qSketchRegion(id+"F23",true);
            extrude(context, id + "F25", {"entities" : qUnion([Q0]), "operationType" : NewBodyOperationType.ADD, "depth" : 10 * mm});
        }
        {
            var Q0;
            Q0=makeQuery(id+"F1.opExtrude","SWEPT_FACE",FACE,{"disambiguationData":[OSD([sQuery(id+"F0.wireOp",EDGE,"E21.MirrorCS")])]});
            var sketch = newSketch(context, id + "F26", { "sketchPlane" : qUnion([Q0])});
            skLineSegment(sketch, "E110", {"start": v(-218.82, 19.3) * mm, "end": v(-210.27, 15.92) * mm});
            skLineSegment(sketch, "E111", {"start": v(-210.27, 15.92) * mm, "end": v(-200.88, 18.87) * mm});
            skLineSegment(sketch, "E112", {"start": v(-200.88, 18.87) * mm, "end": v(-193.28, 16) * mm});
            skLineSegment(sketch, "E113", {"start": v(-193.28, 16) * mm, "end": v(-184.53, 19.67) * mm});
            skLineSegment(sketch, "E114", {"start": v(-184.53, 19.67) * mm, "end": v(-218.82, 19.3) * mm});
            skSolve(sketch);
        }
        {
            var Q0;
            Q0=makeQuery(id+"F26.imprint","IMPRINT",FACE,{"disambiguationData":[TD([[makeQuery(id+"F26.imprint","IMPRINT",EDGE,{"derivedFrom":sQuery(id+"F26.wireOp",EDGE,"E110")}),1.0]])]});
            extrude(context, id + "F27", {"entities" : qUnion([Q0]), "operationType" : NewBodyOperationType.REMOVE, "endBound" : BoundingType.SYMMETRIC, "oppositeDirection" : true, "depth" : 40 * mm});
        }
        {
            var Q0;
            Q0=makeQuery(id+"F18.boolean.opBoolean","COPY",FACE,{"derivedFrom":makeQuery(id+"F18.opExtrude","SWEPT_FACE",FACE,{"disambiguationData":[OSD([sQuery(id+"F17.wireOp",EDGE,"E70.5.0")])]})});
            var sketch = newSketch(context, id + "F28", { "sketchPlane" : qUnion([Q0])});
            skLineSegment(sketch, "E115", {"start": v(-0.14, -4.72) * mm, "end": v(-0.14, -19.72) * mm});
            skPoint(sketch, "E115.endSnap0", {"position": v(-0.14, -4.72) * mm});
            skLineSegment(sketch, "E116", {"start": v(-0.14, -4.72) * mm, "end": v(-0.14, 10.28) * mm});
            skLineSegment(sketch, "E117", {"start": v(-0.14, 10.28) * mm, "end": v(-0.14, -19.72) * mm});
            skArc(sketch, "E118", {"start": v(-0.14, -19.72) * mm, "mid": v(14.86, -4.72) * mm, "end": v(-0.14, 10.28) * mm});
            skCircle(sketch, "E119", {"center": v(-0.14, -4.72) * mm, "radius": 13.75 * mm});
            skSolve(sketch);
        }
        {
            var Q0;
            {var subQ0=sQuery(id+"F28.wireOp",EDGE,"E118");Q0=makeQuery(id+"F28.imprint","IMPRINT",FACE,{"disambiguationData":[TD([[makeQuery(id+"F28.imprint","IMPRINT",EDGE,{"derivedFrom":subQ0}),1.0]])]});}
            var Q1;
            Q1=sQuery(id+"F28.wireOp",EDGE,"E117");
            revolve(context, id + "F29", {"entities" : qUnion([Q0]), "axis" : qUnion([Q1]), "revolveType" : RevolveType.ONE_DIRECTION, "oppositeDirection" : true, "angle" : 180 * degree});
        }
    });
